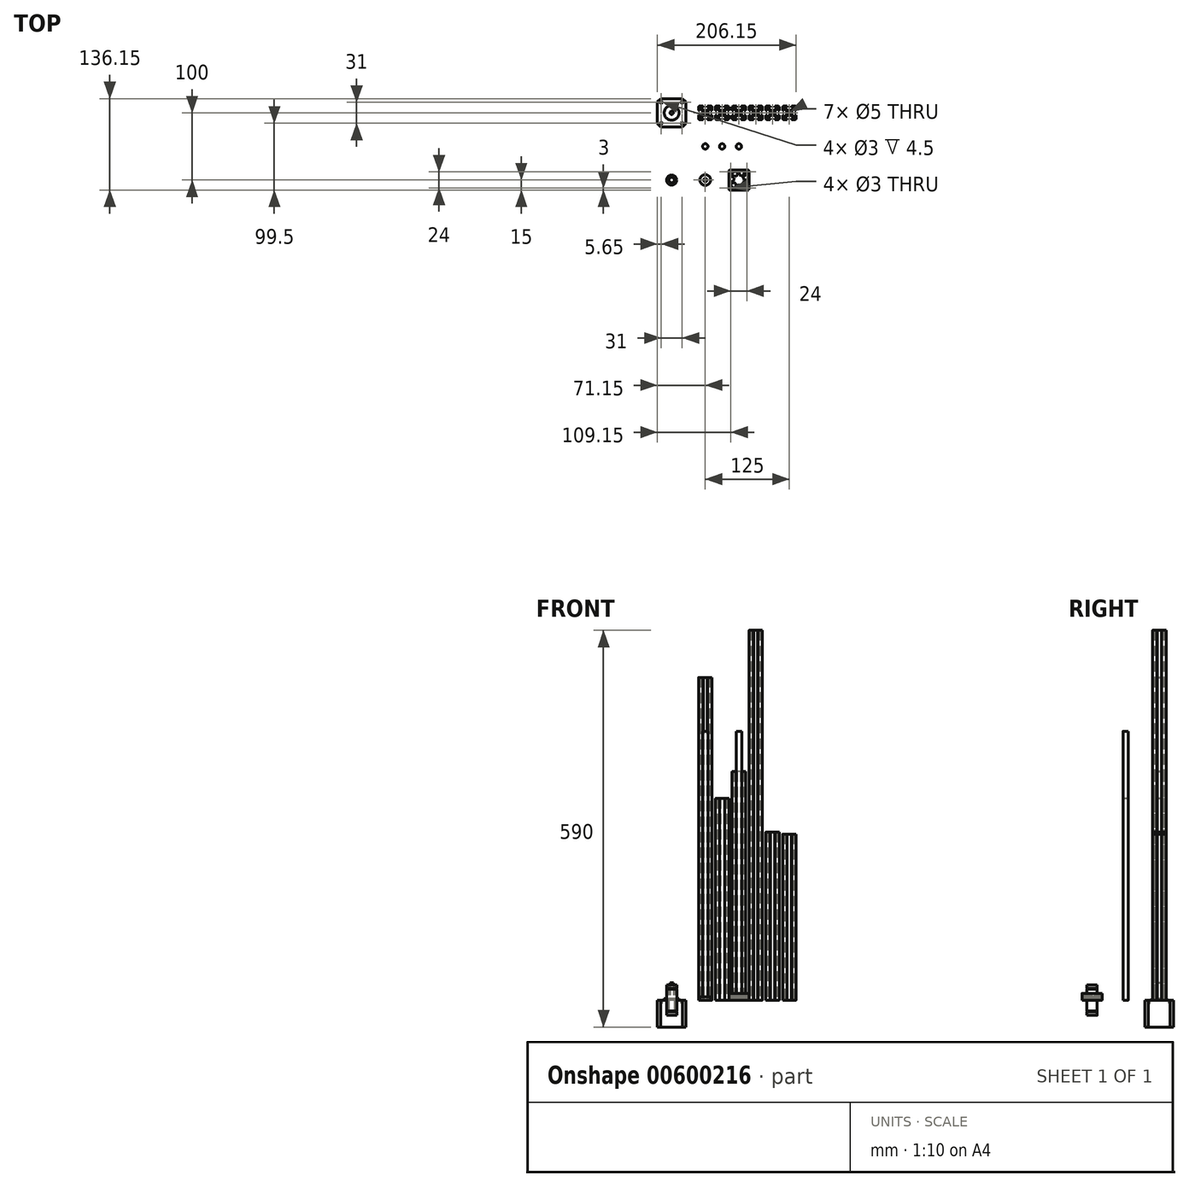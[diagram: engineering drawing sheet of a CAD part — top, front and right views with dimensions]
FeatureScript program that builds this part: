
annotation { "Feature Type Name" : "Feature", "Feature Type Description" : "" }
export const myFeature = defineFeature(function(context is Context, id is Id, definition is map)
    precondition{}
    {
        {
            assignVariable(context, id + "F0", {"name" : "X", "anyValue" : 480});
        }
        {
            assignVariable(context, id + "F1", {"name" : "Y", "anyValue" : 300});
        }
        {
            assignVariable(context, id + "F2", {"name" : "Z", "anyValue" : 550});
        }
        {
            var Q0;
            Q0=qCreatedBy(makeId("Top.planeOp"),FACE);
            var sketch = newSketch(context, id + "F3", { "sketchPlane" : qUnion([Q0])});
            skLineSegment(sketch, "E0.bottom", {"start": v(8.5, -10) * mm, "end": v(-8.5, -10) * mm});
            skLineSegment(sketch, "E0.top", {"start": v(8.5, 10) * mm, "end": v(-8.5, 10) * mm});
            skLineSegment(sketch, "E0.left", {"start": v(10, -8.5) * mm, "end": v(10, 8.5) * mm});
            skLineSegment(sketch, "E0.right", {"start": v(-10, -8.5) * mm, "end": v(-10, 8.5) * mm});
            skPoint(sketch, "E0.middle", {"position": v(0, 0) * mm});
            skPoint(sketch, "E1.visualSharp", {"position": v(-10, 10) * mm});
            skArc(sketch, "E1.filletArc", {"start": v(-8.5, 10) * mm, "mid": v(-9.56, 9.56) * mm, "end": v(-10, 8.5) * mm});
            skPoint(sketch, "E2.visualSharp", {"position": v(10, 10) * mm});
            skArc(sketch, "E2.filletArc", {"start": v(10, 8.5) * mm, "mid": v(9.56, 9.56) * mm, "end": v(8.5, 10) * mm});
            skPoint(sketch, "E3.visualSharp", {"position": v(10, -10) * mm});
            skArc(sketch, "E3.filletArc", {"start": v(8.5, -10) * mm, "mid": v(9.56, -9.56) * mm, "end": v(10, -8.5) * mm});
            skPoint(sketch, "E4.visualSharp", {"position": v(-10, -10) * mm});
            skArc(sketch, "E4.filletArc", {"start": v(-10, -8.5) * mm, "mid": v(-9.56, -9.56) * mm, "end": v(-8.5, -10) * mm});
            skCircle(sketch, "E5", {"center": v(0, 0) * mm, "radius": 2.5 * mm});
            skLineSegment(sketch, "E6", {"start": v(-3.6, -10) * mm, "end": v(-3.6, -9.7) * mm});
            skLineSegment(sketch, "E7", {"start": v(-3.4, -9.5) * mm, "end": v(-3.1, -9.5) * mm});
            skLineSegment(sketch, "E8", {"start": v(-3.1, -9.5) * mm, "end": v(-3.1, -8.2) * mm});
            skLineSegment(sketch, "E9", {"start": v(-3.1, -8.2) * mm, "end": v(-5.5, -8.2) * mm});
            skLineSegment(sketch, "E10", {"start": v(-3.43, -4.49) * mm, "end": v(-5.5, -6.56) * mm});
            skLineSegment(sketch, "E11", {"start": v(-2.01, -3.9) * mm, "end": v(2.01, -3.9) * mm});
            skLineSegment(sketch, "E12", {"start": v(5.5, -6.56) * mm, "end": v(3.43, -4.49) * mm});
            skLineSegment(sketch, "E13", {"start": v(5.5, -8.2) * mm, "end": v(3.1, -8.2) * mm});
            skLineSegment(sketch, "E14", {"start": v(3.1, -8.2) * mm, "end": v(3.1, -9.5) * mm});
            skLineSegment(sketch, "E15", {"start": v(3.1, -9.5) * mm, "end": v(3.4, -9.5) * mm});
            skLineSegment(sketch, "E16", {"start": v(3.6, -9.7) * mm, "end": v(3.6, -10) * mm});
            skLineSegment(sketch, "E17", {"start": v(0, 0) * mm, "end": v(0, -10) * mm, "construction": true});
            skLineSegment(sketch, "E18", {"start": v(5.5, -6.56) * mm, "end": v(5.5, -8.2) * mm});
            skLineSegment(sketch, "E19", {"start": v(-5.5, -6.56) * mm, "end": v(-5.5, -8.2) * mm});
            skPoint(sketch, "E20.visualSharp", {"position": v(-2.84, -3.9) * mm});
            skArc(sketch, "E20.filletArc", {"start": v(-2.01, -3.9) * mm, "mid": v(-2.78, -4.05) * mm, "end": v(-3.43, -4.49) * mm});
            skPoint(sketch, "E21.visualSharp", {"position": v(2.84, -3.9) * mm});
            skArc(sketch, "E21.filletArc", {"start": v(3.43, -4.49) * mm, "mid": v(2.78, -4.05) * mm, "end": v(2.01, -3.9) * mm});
            skPoint(sketch, "E22.visualSharp", {"position": v(-3.6, -9.5) * mm});
            skArc(sketch, "E22.filletArc", {"start": v(-3.4, -9.5) * mm, "mid": v(-3.54, -9.56) * mm, "end": v(-3.6, -9.7) * mm});
            skPoint(sketch, "E23.visualSharp", {"position": v(3.6, -9.5) * mm});
            skArc(sketch, "E23.filletArc", {"start": v(3.6, -9.7) * mm, "mid": v(3.54, -9.56) * mm, "end": v(3.4, -9.5) * mm});
            skLineSegment(sketch, "E24.1.0", {"start": v(6.56, 5.5) * mm, "end": v(4.49, 3.43) * mm});
            skLineSegment(sketch, "E24.1.1", {"start": v(3.9, -2.01) * mm, "end": v(3.9, 2.01) * mm});
            skLineSegment(sketch, "E24.1.2", {"start": v(6.56, 5.5) * mm, "end": v(8.2, 5.5) * mm});
            skArc(sketch, "E24.1.3", {"start": v(4.49, 3.43) * mm, "mid": v(4.05, 2.78) * mm, "end": v(3.9, 2.01) * mm});
            skLineSegment(sketch, "E24.1.4", {"start": v(8.2, 3.1) * mm, "end": v(9.5, 3.1) * mm});
            skPoint(sketch, "E24.1.5", {"position": v(3.9, -2.84) * mm});
            skPoint(sketch, "E24.1.6", {"position": v(9.5, -3.6) * mm});
            skPoint(sketch, "E24.1.7", {"position": v(9.5, 3.6) * mm});
            skLineSegment(sketch, "E24.1.8", {"start": v(8.2, -3.1) * mm, "end": v(8.2, -5.5) * mm});
            skLineSegment(sketch, "E24.1.9", {"start": v(9.7, 3.6) * mm, "end": v(10, 3.6) * mm});
            skLineSegment(sketch, "E24.1.10", {"start": v(9.5, -3.1) * mm, "end": v(8.2, -3.1) * mm});
            skLineSegment(sketch, "E24.1.11", {"start": v(8.2, 5.5) * mm, "end": v(8.2, 3.1) * mm});
            skLineSegment(sketch, "E24.1.12", {"start": v(4.49, -3.43) * mm, "end": v(6.56, -5.5) * mm});
            skPoint(sketch, "E24.1.13", {"position": v(3.9, 2.84) * mm});
            skLineSegment(sketch, "E24.1.14", {"start": v(6.56, -5.5) * mm, "end": v(8.2, -5.5) * mm});
            skLineSegment(sketch, "E24.1.15", {"start": v(9.5, 3.1) * mm, "end": v(9.5, 3.4) * mm});
            skLineSegment(sketch, "E24.1.16", {"start": v(9.5, -3.4) * mm, "end": v(9.5, -3.1) * mm});
            skArc(sketch, "E24.1.17", {"start": v(3.9, -2.01) * mm, "mid": v(4.05, -2.78) * mm, "end": v(4.49, -3.43) * mm});
            skLineSegment(sketch, "E24.1.18", {"start": v(10, -3.6) * mm, "end": v(9.7, -3.6) * mm});
            skArc(sketch, "E24.1.19", {"start": v(9.5, -3.4) * mm, "mid": v(9.56, -3.54) * mm, "end": v(9.7, -3.6) * mm});
            skArc(sketch, "E24.1.20", {"start": v(9.7, 3.6) * mm, "mid": v(9.56, 3.54) * mm, "end": v(9.5, 3.4) * mm});
            skLineSegment(sketch, "E24.2.0", {"start": v(-5.5, 6.56) * mm, "end": v(-3.43, 4.49) * mm});
            skLineSegment(sketch, "E24.2.1", {"start": v(2.01, 3.9) * mm, "end": v(-2.01, 3.9) * mm});
            skLineSegment(sketch, "E24.2.2", {"start": v(-5.5, 6.56) * mm, "end": v(-5.5, 8.2) * mm});
            skArc(sketch, "E24.2.3", {"start": v(-3.43, 4.49) * mm, "mid": v(-2.78, 4.05) * mm, "end": v(-2.01, 3.9) * mm});
            skLineSegment(sketch, "E24.2.4", {"start": v(-3.1, 8.2) * mm, "end": v(-3.1, 9.5) * mm});
            skPoint(sketch, "E24.2.5", {"position": v(2.84, 3.9) * mm});
            skPoint(sketch, "E24.2.6", {"position": v(3.6, 9.5) * mm});
            skPoint(sketch, "E24.2.7", {"position": v(-3.6, 9.5) * mm});
            skLineSegment(sketch, "E24.2.8", {"start": v(3.1, 8.2) * mm, "end": v(5.5, 8.2) * mm});
            skLineSegment(sketch, "E24.2.9", {"start": v(-3.6, 9.7) * mm, "end": v(-3.6, 10) * mm});
            skLineSegment(sketch, "E24.2.10", {"start": v(3.1, 9.5) * mm, "end": v(3.1, 8.2) * mm});
            skLineSegment(sketch, "E24.2.11", {"start": v(-5.5, 8.2) * mm, "end": v(-3.1, 8.2) * mm});
            skLineSegment(sketch, "E24.2.12", {"start": v(3.43, 4.49) * mm, "end": v(5.5, 6.56) * mm});
            skPoint(sketch, "E24.2.13", {"position": v(-2.84, 3.9) * mm});
            skLineSegment(sketch, "E24.2.14", {"start": v(5.5, 6.56) * mm, "end": v(5.5, 8.2) * mm});
            skLineSegment(sketch, "E24.2.15", {"start": v(-3.1, 9.5) * mm, "end": v(-3.4, 9.5) * mm});
            skLineSegment(sketch, "E24.2.16", {"start": v(3.4, 9.5) * mm, "end": v(3.1, 9.5) * mm});
            skArc(sketch, "E24.2.17", {"start": v(2.01, 3.9) * mm, "mid": v(2.78, 4.05) * mm, "end": v(3.43, 4.49) * mm});
            skLineSegment(sketch, "E24.2.18", {"start": v(3.6, 10) * mm, "end": v(3.6, 9.7) * mm});
            skArc(sketch, "E24.2.19", {"start": v(3.4, 9.5) * mm, "mid": v(3.54, 9.56) * mm, "end": v(3.6, 9.7) * mm});
            skArc(sketch, "E24.2.20", {"start": v(-3.6, 9.7) * mm, "mid": v(-3.54, 9.56) * mm, "end": v(-3.4, 9.5) * mm});
            skLineSegment(sketch, "E24.3.0", {"start": v(-6.56, -5.5) * mm, "end": v(-4.49, -3.43) * mm});
            skLineSegment(sketch, "E24.3.1", {"start": v(-3.9, 2.01) * mm, "end": v(-3.9, -2.01) * mm});
            skLineSegment(sketch, "E24.3.2", {"start": v(-6.56, -5.5) * mm, "end": v(-8.2, -5.5) * mm});
            skArc(sketch, "E24.3.3", {"start": v(-4.49, -3.43) * mm, "mid": v(-4.05, -2.78) * mm, "end": v(-3.9, -2.01) * mm});
            skLineSegment(sketch, "E24.3.4", {"start": v(-8.2, -3.1) * mm, "end": v(-9.5, -3.1) * mm});
            skPoint(sketch, "E24.3.5", {"position": v(-3.9, 2.84) * mm});
            skPoint(sketch, "E24.3.6", {"position": v(-9.5, 3.6) * mm});
            skPoint(sketch, "E24.3.7", {"position": v(-9.5, -3.6) * mm});
            skLineSegment(sketch, "E24.3.8", {"start": v(-8.2, 3.1) * mm, "end": v(-8.2, 5.5) * mm});
            skLineSegment(sketch, "E24.3.9", {"start": v(-9.7, -3.6) * mm, "end": v(-10, -3.6) * mm});
            skLineSegment(sketch, "E24.3.10", {"start": v(-9.5, 3.1) * mm, "end": v(-8.2, 3.1) * mm});
            skLineSegment(sketch, "E24.3.11", {"start": v(-8.2, -5.5) * mm, "end": v(-8.2, -3.1) * mm});
            skLineSegment(sketch, "E24.3.12", {"start": v(-4.49, 3.43) * mm, "end": v(-6.56, 5.5) * mm});
            skPoint(sketch, "E24.3.13", {"position": v(-3.9, -2.84) * mm});
            skLineSegment(sketch, "E24.3.14", {"start": v(-6.56, 5.5) * mm, "end": v(-8.2, 5.5) * mm});
            skLineSegment(sketch, "E24.3.15", {"start": v(-9.5, -3.1) * mm, "end": v(-9.5, -3.4) * mm});
            skLineSegment(sketch, "E24.3.16", {"start": v(-9.5, 3.4) * mm, "end": v(-9.5, 3.1) * mm});
            skArc(sketch, "E24.3.17", {"start": v(-3.9, 2.01) * mm, "mid": v(-4.05, 2.78) * mm, "end": v(-4.49, 3.43) * mm});
            skLineSegment(sketch, "E24.3.18", {"start": v(-10, 3.6) * mm, "end": v(-9.7, 3.6) * mm});
            skArc(sketch, "E24.3.19", {"start": v(-9.5, 3.4) * mm, "mid": v(-9.56, 3.54) * mm, "end": v(-9.7, 3.6) * mm});
            skArc(sketch, "E24.3.20", {"start": v(-9.7, -3.6) * mm, "mid": v(-9.56, -3.54) * mm, "end": v(-9.5, -3.4) * mm});
            skLineSegment(sketch, "E25.1.0.0", {"start": v(33.5, 10) * mm, "end": v(16.5, 10) * mm});
            skLineSegment(sketch, "E25.1.0.1", {"start": v(35, -8.5) * mm, "end": v(35, 8.5) * mm});
            skLineSegment(sketch, "E25.1.0.2", {"start": v(33.5, -10) * mm, "end": v(16.5, -10) * mm});
            skLineSegment(sketch, "E25.1.0.3", {"start": v(30.5, -6.56) * mm, "end": v(28.43, -4.49) * mm});
            skLineSegment(sketch, "E25.1.0.4", {"start": v(15, -8.5) * mm, "end": v(15, 8.5) * mm});
            skPoint(sketch, "E25.1.0.5", {"position": v(15, 10) * mm});
            skPoint(sketch, "E25.1.0.6", {"position": v(35, -10) * mm});
            skCircle(sketch, "E25.1.0.7", {"center": v(25, 0) * mm, "radius": 2.5 * mm});
            skLineSegment(sketch, "E25.1.0.8", {"start": v(28.1, 8.2) * mm, "end": v(30.5, 8.2) * mm});
            skPoint(sketch, "E25.1.0.9", {"position": v(21.1, -2.84) * mm});
            skPoint(sketch, "E25.1.0.10", {"position": v(28.9, 2.84) * mm});
            skLineSegment(sketch, "E25.1.0.11", {"start": v(18.44, -5.5) * mm, "end": v(20.51, -3.43) * mm});
            skLineSegment(sketch, "E25.1.0.12", {"start": v(30.5, -8.2) * mm, "end": v(28.1, -8.2) * mm});
            skPoint(sketch, "E25.1.0.13", {"position": v(15, -10) * mm});
            skLineSegment(sketch, "E25.1.0.14", {"start": v(22.99, -3.9) * mm, "end": v(27.01, -3.9) * mm});
            skLineSegment(sketch, "E25.1.0.15", {"start": v(27.01, 3.9) * mm, "end": v(22.99, 3.9) * mm});
            skLineSegment(sketch, "E25.1.0.16", {"start": v(31.56, 5.5) * mm, "end": v(29.49, 3.43) * mm});
            skPoint(sketch, "E25.1.0.17", {"position": v(15.5, 3.6) * mm});
            skPoint(sketch, "E25.1.0.18", {"position": v(34.5, -3.6) * mm});
            skLineSegment(sketch, "E25.1.0.19", {"start": v(33.2, -3.1) * mm, "end": v(33.2, -5.5) * mm});
            skLineSegment(sketch, "E25.1.0.20", {"start": v(21.57, -4.49) * mm, "end": v(19.5, -6.56) * mm});
            skPoint(sketch, "E25.1.0.21", {"position": v(15.5, -3.6) * mm});
            skPoint(sketch, "E25.1.0.22", {"position": v(34.5, 3.6) * mm});
            skLineSegment(sketch, "E25.1.0.23", {"start": v(19.5, 6.56) * mm, "end": v(21.57, 4.49) * mm});
            skLineSegment(sketch, "E25.1.0.24", {"start": v(28.9, -2.01) * mm, "end": v(28.9, 2.01) * mm});
            skLineSegment(sketch, "E25.1.0.25", {"start": v(21.1, 2.01) * mm, "end": v(21.1, -2.01) * mm});
            skLineSegment(sketch, "E25.1.0.26", {"start": v(16.8, 3.1) * mm, "end": v(16.8, 5.5) * mm});
            skPoint(sketch, "E25.1.0.27", {"position": v(35, 10) * mm});
            skPoint(sketch, "E25.1.0.28", {"position": v(28.9, -2.84) * mm});
            skPoint(sketch, "E25.1.0.29", {"position": v(21.1, 2.84) * mm});
            skPoint(sketch, "E25.1.0.30", {"position": v(25, 0) * mm});
            skPoint(sketch, "E25.1.0.31", {"position": v(28.6, -9.5) * mm});
            skPoint(sketch, "E25.1.0.32", {"position": v(22.16, 3.9) * mm});
            skPoint(sketch, "E25.1.0.33", {"position": v(21.4, 9.5) * mm});
            skLineSegment(sketch, "E25.1.0.34", {"start": v(20.51, 3.43) * mm, "end": v(18.44, 5.5) * mm});
            skPoint(sketch, "E25.1.0.35", {"position": v(27.84, -3.9) * mm});
            skPoint(sketch, "E25.1.0.36", {"position": v(28.6, 9.5) * mm});
            skLineSegment(sketch, "E25.1.0.37", {"start": v(28.43, 4.49) * mm, "end": v(30.5, 6.56) * mm});
            skLineSegment(sketch, "E25.1.0.38", {"start": v(16.8, -5.5) * mm, "end": v(16.8, -3.1) * mm});
            skPoint(sketch, "E25.1.0.39", {"position": v(27.84, 3.9) * mm});
            skLineSegment(sketch, "E25.1.0.40", {"start": v(29.49, -3.43) * mm, "end": v(31.56, -5.5) * mm});
            skLineSegment(sketch, "E25.1.0.41", {"start": v(19.5, 8.2) * mm, "end": v(21.9, 8.2) * mm});
            skLineSegment(sketch, "E25.1.0.42", {"start": v(25, 0) * mm, "end": v(25, -10) * mm, "construction": true});
            skPoint(sketch, "E25.1.0.43", {"position": v(22.16, -3.9) * mm});
            skLineSegment(sketch, "E25.1.0.44", {"start": v(33.2, 5.5) * mm, "end": v(33.2, 3.1) * mm});
            skArc(sketch, "E25.1.0.45", {"start": v(35, 8.5) * mm, "mid": v(34.56, 9.56) * mm, "end": v(33.5, 10) * mm});
            skArc(sketch, "E25.1.0.46", {"start": v(16.5, 10) * mm, "mid": v(15.44, 9.56) * mm, "end": v(15, 8.5) * mm});
            skLineSegment(sketch, "E25.1.0.47", {"start": v(21.9, -8.2) * mm, "end": v(19.5, -8.2) * mm});
            skArc(sketch, "E25.1.0.48", {"start": v(33.5, -10) * mm, "mid": v(34.56, -9.56) * mm, "end": v(35, -8.5) * mm});
            skArc(sketch, "E25.1.0.49", {"start": v(15, -8.5) * mm, "mid": v(15.44, -9.56) * mm, "end": v(16.5, -10) * mm});
            skPoint(sketch, "E25.1.0.50", {"position": v(21.4, -9.5) * mm});
            skPoint(sketch, "E25.1.0.51", {"position": v(25, 0) * mm});
            skLineSegment(sketch, "E25.1.0.52", {"start": v(28.1, -8.2) * mm, "end": v(28.1, -9.5) * mm});
            skLineSegment(sketch, "E25.1.0.53", {"start": v(16.8, -3.1) * mm, "end": v(15.5, -3.1) * mm});
            skLineSegment(sketch, "E25.1.0.54", {"start": v(18.44, -5.5) * mm, "end": v(16.8, -5.5) * mm});
            skArc(sketch, "E25.1.0.55", {"start": v(20.51, -3.43) * mm, "mid": v(20.95, -2.78) * mm, "end": v(21.1, -2.01) * mm});
            skLineSegment(sketch, "E25.1.0.56", {"start": v(21.9, 8.2) * mm, "end": v(21.9, 9.5) * mm});
            skLineSegment(sketch, "E25.1.0.57", {"start": v(33.2, 3.1) * mm, "end": v(34.5, 3.1) * mm});
            skLineSegment(sketch, "E25.1.0.58", {"start": v(31.56, 5.5) * mm, "end": v(33.2, 5.5) * mm});
            skArc(sketch, "E25.1.0.59", {"start": v(21.57, 4.49) * mm, "mid": v(22.22, 4.05) * mm, "end": v(22.99, 3.9) * mm});
            skLineSegment(sketch, "E25.1.0.60", {"start": v(19.5, 6.56) * mm, "end": v(19.5, 8.2) * mm});
            skLineSegment(sketch, "E25.1.0.61", {"start": v(34.5, -3.1) * mm, "end": v(33.2, -3.1) * mm});
            skArc(sketch, "E25.1.0.62", {"start": v(29.49, 3.43) * mm, "mid": v(29.05, 2.78) * mm, "end": v(28.9, 2.01) * mm});
            skArc(sketch, "E25.1.0.63", {"start": v(21.1, 2.01) * mm, "mid": v(20.95, 2.78) * mm, "end": v(20.51, 3.43) * mm});
            skArc(sketch, "E25.1.0.64", {"start": v(27.01, 3.9) * mm, "mid": v(27.78, 4.05) * mm, "end": v(28.43, 4.49) * mm});
            skArc(sketch, "E25.1.0.65", {"start": v(28.43, -4.49) * mm, "mid": v(27.78, -4.05) * mm, "end": v(27.01, -3.9) * mm});
            skArc(sketch, "E25.1.0.66", {"start": v(28.9, -2.01) * mm, "mid": v(29.05, -2.78) * mm, "end": v(29.49, -3.43) * mm});
            skLineSegment(sketch, "E25.1.0.67", {"start": v(18.44, 5.5) * mm, "end": v(16.8, 5.5) * mm});
            skArc(sketch, "E25.1.0.68", {"start": v(22.99, -3.9) * mm, "mid": v(22.22, -4.05) * mm, "end": v(21.57, -4.49) * mm});
            skLineSegment(sketch, "E25.1.0.69", {"start": v(30.5, 6.56) * mm, "end": v(30.5, 8.2) * mm});
            skLineSegment(sketch, "E25.1.0.70", {"start": v(19.5, -6.56) * mm, "end": v(19.5, -8.2) * mm});
            skLineSegment(sketch, "E25.1.0.71", {"start": v(31.56, -5.5) * mm, "end": v(33.2, -5.5) * mm});
            skLineSegment(sketch, "E25.1.0.72", {"start": v(30.5, -6.56) * mm, "end": v(30.5, -8.2) * mm});
            skLineSegment(sketch, "E25.1.0.73", {"start": v(15.5, 3.1) * mm, "end": v(16.8, 3.1) * mm});
            skLineSegment(sketch, "E25.1.0.74", {"start": v(28.1, 9.5) * mm, "end": v(28.1, 8.2) * mm});
            skLineSegment(sketch, "E25.1.0.75", {"start": v(21.9, -9.5) * mm, "end": v(21.9, -8.2) * mm});
            skArc(sketch, "E25.1.0.76", {"start": v(34.5, -3.4) * mm, "mid": v(34.56, -3.54) * mm, "end": v(34.7, -3.6) * mm});
            skLineSegment(sketch, "E25.1.0.77", {"start": v(35, -3.6) * mm, "end": v(34.7, -3.6) * mm});
            skLineSegment(sketch, "E25.1.0.78", {"start": v(34.5, -3.4) * mm, "end": v(34.5, -3.1) * mm});
            skArc(sketch, "E25.1.0.79", {"start": v(15.3, -3.6) * mm, "mid": v(15.44, -3.54) * mm, "end": v(15.5, -3.4) * mm});
            skArc(sketch, "E25.1.0.80", {"start": v(28.4, 9.5) * mm, "mid": v(28.54, 9.56) * mm, "end": v(28.6, 9.7) * mm});
            skLineSegment(sketch, "E25.1.0.81", {"start": v(28.1, -9.5) * mm, "end": v(28.4, -9.5) * mm});
            skArc(sketch, "E25.1.0.82", {"start": v(28.6, -9.7) * mm, "mid": v(28.54, -9.56) * mm, "end": v(28.4, -9.5) * mm});
            skLineSegment(sketch, "E25.1.0.83", {"start": v(28.6, 10) * mm, "end": v(28.6, 9.7) * mm});
            skLineSegment(sketch, "E25.1.0.84", {"start": v(15.5, -3.1) * mm, "end": v(15.5, -3.4) * mm});
            skLineSegment(sketch, "E25.1.0.85", {"start": v(28.4, 9.5) * mm, "end": v(28.1, 9.5) * mm});
            skLineSegment(sketch, "E25.1.0.86", {"start": v(15.3, -3.6) * mm, "end": v(15, -3.6) * mm});
            skLineSegment(sketch, "E25.1.0.87", {"start": v(28.6, -9.7) * mm, "end": v(28.6, -10) * mm});
            skArc(sketch, "E25.1.0.88", {"start": v(21.4, 9.7) * mm, "mid": v(21.46, 9.56) * mm, "end": v(21.6, 9.5) * mm});
            skLineSegment(sketch, "E25.1.0.89", {"start": v(21.4, -10) * mm, "end": v(21.4, -9.7) * mm});
            skLineSegment(sketch, "E25.1.0.90", {"start": v(21.6, -9.5) * mm, "end": v(21.9, -9.5) * mm});
            skLineSegment(sketch, "E25.1.0.91", {"start": v(21.4, 9.7) * mm, "end": v(21.4, 10) * mm});
            skLineSegment(sketch, "E25.1.0.92", {"start": v(21.9, 9.5) * mm, "end": v(21.6, 9.5) * mm});
            skLineSegment(sketch, "E25.1.0.93", {"start": v(15, 3.6) * mm, "end": v(15.3, 3.6) * mm});
            skArc(sketch, "E25.1.0.94", {"start": v(34.7, 3.6) * mm, "mid": v(34.56, 3.54) * mm, "end": v(34.5, 3.4) * mm});
            skArc(sketch, "E25.1.0.95", {"start": v(15.5, 3.4) * mm, "mid": v(15.44, 3.54) * mm, "end": v(15.3, 3.6) * mm});
            skLineSegment(sketch, "E25.1.0.96", {"start": v(34.7, 3.6) * mm, "end": v(35, 3.6) * mm});
            skLineSegment(sketch, "E25.1.0.97", {"start": v(15.5, 3.4) * mm, "end": v(15.5, 3.1) * mm});
            skArc(sketch, "E25.1.0.98", {"start": v(21.6, -9.5) * mm, "mid": v(21.46, -9.56) * mm, "end": v(21.4, -9.7) * mm});
            skLineSegment(sketch, "E25.1.0.99", {"start": v(34.5, 3.1) * mm, "end": v(34.5, 3.4) * mm});
            skLineSegment(sketch, "E25.2.0.0", {"start": v(58.5, 10) * mm, "end": v(41.5, 10) * mm});
            skLineSegment(sketch, "E25.2.0.1", {"start": v(60, -8.5) * mm, "end": v(60, 8.5) * mm});
            skLineSegment(sketch, "E25.2.0.2", {"start": v(58.5, -10) * mm, "end": v(41.5, -10) * mm});
            skLineSegment(sketch, "E25.2.0.3", {"start": v(55.5, -6.56) * mm, "end": v(53.43, -4.49) * mm});
            skLineSegment(sketch, "E25.2.0.4", {"start": v(40, -8.5) * mm, "end": v(40, 8.5) * mm});
            skPoint(sketch, "E25.2.0.5", {"position": v(40, 10) * mm});
            skPoint(sketch, "E25.2.0.6", {"position": v(60, -10) * mm});
            skCircle(sketch, "E25.2.0.7", {"center": v(50, 0) * mm, "radius": 2.5 * mm});
            skLineSegment(sketch, "E25.2.0.8", {"start": v(53.1, 8.2) * mm, "end": v(55.5, 8.2) * mm});
            skPoint(sketch, "E25.2.0.9", {"position": v(46.1, -2.84) * mm});
            skPoint(sketch, "E25.2.0.10", {"position": v(53.9, 2.84) * mm});
            skLineSegment(sketch, "E25.2.0.11", {"start": v(43.44, -5.5) * mm, "end": v(45.51, -3.43) * mm});
            skLineSegment(sketch, "E25.2.0.12", {"start": v(55.5, -8.2) * mm, "end": v(53.1, -8.2) * mm});
            skPoint(sketch, "E25.2.0.13", {"position": v(40, -10) * mm});
            skLineSegment(sketch, "E25.2.0.14", {"start": v(47.99, -3.9) * mm, "end": v(52.01, -3.9) * mm});
            skLineSegment(sketch, "E25.2.0.15", {"start": v(52.01, 3.9) * mm, "end": v(47.99, 3.9) * mm});
            skLineSegment(sketch, "E25.2.0.16", {"start": v(56.56, 5.5) * mm, "end": v(54.49, 3.43) * mm});
            skPoint(sketch, "E25.2.0.17", {"position": v(40.5, 3.6) * mm});
            skPoint(sketch, "E25.2.0.18", {"position": v(59.5, -3.6) * mm});
            skLineSegment(sketch, "E25.2.0.19", {"start": v(58.2, -3.1) * mm, "end": v(58.2, -5.5) * mm});
            skLineSegment(sketch, "E25.2.0.20", {"start": v(46.57, -4.49) * mm, "end": v(44.5, -6.56) * mm});
            skPoint(sketch, "E25.2.0.21", {"position": v(40.5, -3.6) * mm});
            skPoint(sketch, "E25.2.0.22", {"position": v(59.5, 3.6) * mm});
            skLineSegment(sketch, "E25.2.0.23", {"start": v(44.5, 6.56) * mm, "end": v(46.57, 4.49) * mm});
            skLineSegment(sketch, "E25.2.0.24", {"start": v(53.9, -2.01) * mm, "end": v(53.9, 2.01) * mm});
            skLineSegment(sketch, "E25.2.0.25", {"start": v(46.1, 2.01) * mm, "end": v(46.1, -2.01) * mm});
            skLineSegment(sketch, "E25.2.0.26", {"start": v(41.8, 3.1) * mm, "end": v(41.8, 5.5) * mm});
            skPoint(sketch, "E25.2.0.27", {"position": v(60, 10) * mm});
            skPoint(sketch, "E25.2.0.28", {"position": v(53.9, -2.84) * mm});
            skPoint(sketch, "E25.2.0.29", {"position": v(46.1, 2.84) * mm});
            skPoint(sketch, "E25.2.0.30", {"position": v(50, 0) * mm});
            skPoint(sketch, "E25.2.0.31", {"position": v(53.6, -9.5) * mm});
            skPoint(sketch, "E25.2.0.32", {"position": v(47.16, 3.9) * mm});
            skPoint(sketch, "E25.2.0.33", {"position": v(46.4, 9.5) * mm});
            skLineSegment(sketch, "E25.2.0.34", {"start": v(45.51, 3.43) * mm, "end": v(43.44, 5.5) * mm});
            skPoint(sketch, "E25.2.0.35", {"position": v(52.84, -3.9) * mm});
            skPoint(sketch, "E25.2.0.36", {"position": v(53.6, 9.5) * mm});
            skLineSegment(sketch, "E25.2.0.37", {"start": v(53.43, 4.49) * mm, "end": v(55.5, 6.56) * mm});
            skLineSegment(sketch, "E25.2.0.38", {"start": v(41.8, -5.5) * mm, "end": v(41.8, -3.1) * mm});
            skPoint(sketch, "E25.2.0.39", {"position": v(52.84, 3.9) * mm});
            skLineSegment(sketch, "E25.2.0.40", {"start": v(54.49, -3.43) * mm, "end": v(56.56, -5.5) * mm});
            skLineSegment(sketch, "E25.2.0.41", {"start": v(44.5, 8.2) * mm, "end": v(46.9, 8.2) * mm});
            skLineSegment(sketch, "E25.2.0.42", {"start": v(50, 0) * mm, "end": v(50, -10) * mm, "construction": true});
            skPoint(sketch, "E25.2.0.43", {"position": v(47.16, -3.9) * mm});
            skLineSegment(sketch, "E25.2.0.44", {"start": v(58.2, 5.5) * mm, "end": v(58.2, 3.1) * mm});
            skArc(sketch, "E25.2.0.45", {"start": v(60, 8.5) * mm, "mid": v(59.56, 9.56) * mm, "end": v(58.5, 10) * mm});
            skArc(sketch, "E25.2.0.46", {"start": v(41.5, 10) * mm, "mid": v(40.44, 9.56) * mm, "end": v(40, 8.5) * mm});
            skLineSegment(sketch, "E25.2.0.47", {"start": v(46.9, -8.2) * mm, "end": v(44.5, -8.2) * mm});
            skArc(sketch, "E25.2.0.48", {"start": v(58.5, -10) * mm, "mid": v(59.56, -9.56) * mm, "end": v(60, -8.5) * mm});
            skArc(sketch, "E25.2.0.49", {"start": v(40, -8.5) * mm, "mid": v(40.44, -9.56) * mm, "end": v(41.5, -10) * mm});
            skPoint(sketch, "E25.2.0.50", {"position": v(46.4, -9.5) * mm});
            skPoint(sketch, "E25.2.0.51", {"position": v(50, 0) * mm});
            skLineSegment(sketch, "E25.2.0.52", {"start": v(53.1, -8.2) * mm, "end": v(53.1, -9.5) * mm});
            skLineSegment(sketch, "E25.2.0.53", {"start": v(41.8, -3.1) * mm, "end": v(40.5, -3.1) * mm});
            skLineSegment(sketch, "E25.2.0.54", {"start": v(43.44, -5.5) * mm, "end": v(41.8, -5.5) * mm});
            skArc(sketch, "E25.2.0.55", {"start": v(45.51, -3.43) * mm, "mid": v(45.95, -2.78) * mm, "end": v(46.1, -2.01) * mm});
            skLineSegment(sketch, "E25.2.0.56", {"start": v(46.9, 8.2) * mm, "end": v(46.9, 9.5) * mm});
            skLineSegment(sketch, "E25.2.0.57", {"start": v(58.2, 3.1) * mm, "end": v(59.5, 3.1) * mm});
            skLineSegment(sketch, "E25.2.0.58", {"start": v(56.56, 5.5) * mm, "end": v(58.2, 5.5) * mm});
            skArc(sketch, "E25.2.0.59", {"start": v(46.57, 4.49) * mm, "mid": v(47.22, 4.05) * mm, "end": v(47.99, 3.9) * mm});
            skLineSegment(sketch, "E25.2.0.60", {"start": v(44.5, 6.56) * mm, "end": v(44.5, 8.2) * mm});
            skLineSegment(sketch, "E25.2.0.61", {"start": v(59.5, -3.1) * mm, "end": v(58.2, -3.1) * mm});
            skArc(sketch, "E25.2.0.62", {"start": v(54.49, 3.43) * mm, "mid": v(54.05, 2.78) * mm, "end": v(53.9, 2.01) * mm});
            skArc(sketch, "E25.2.0.63", {"start": v(46.1, 2.01) * mm, "mid": v(45.95, 2.78) * mm, "end": v(45.51, 3.43) * mm});
            skArc(sketch, "E25.2.0.64", {"start": v(52.01, 3.9) * mm, "mid": v(52.78, 4.05) * mm, "end": v(53.43, 4.49) * mm});
            skArc(sketch, "E25.2.0.65", {"start": v(53.43, -4.49) * mm, "mid": v(52.78, -4.05) * mm, "end": v(52.01, -3.9) * mm});
            skArc(sketch, "E25.2.0.66", {"start": v(53.9, -2.01) * mm, "mid": v(54.05, -2.78) * mm, "end": v(54.49, -3.43) * mm});
            skLineSegment(sketch, "E25.2.0.67", {"start": v(43.44, 5.5) * mm, "end": v(41.8, 5.5) * mm});
            skArc(sketch, "E25.2.0.68", {"start": v(47.99, -3.9) * mm, "mid": v(47.22, -4.05) * mm, "end": v(46.57, -4.49) * mm});
            skLineSegment(sketch, "E25.2.0.69", {"start": v(55.5, 6.56) * mm, "end": v(55.5, 8.2) * mm});
            skLineSegment(sketch, "E25.2.0.70", {"start": v(44.5, -6.56) * mm, "end": v(44.5, -8.2) * mm});
            skLineSegment(sketch, "E25.2.0.71", {"start": v(56.56, -5.5) * mm, "end": v(58.2, -5.5) * mm});
            skLineSegment(sketch, "E25.2.0.72", {"start": v(55.5, -6.56) * mm, "end": v(55.5, -8.2) * mm});
            skLineSegment(sketch, "E25.2.0.73", {"start": v(40.5, 3.1) * mm, "end": v(41.8, 3.1) * mm});
            skLineSegment(sketch, "E25.2.0.74", {"start": v(53.1, 9.5) * mm, "end": v(53.1, 8.2) * mm});
            skLineSegment(sketch, "E25.2.0.75", {"start": v(46.9, -9.5) * mm, "end": v(46.9, -8.2) * mm});
            skArc(sketch, "E25.2.0.76", {"start": v(59.5, -3.4) * mm, "mid": v(59.56, -3.54) * mm, "end": v(59.7, -3.6) * mm});
            skLineSegment(sketch, "E25.2.0.77", {"start": v(60, -3.6) * mm, "end": v(59.7, -3.6) * mm});
            skLineSegment(sketch, "E25.2.0.78", {"start": v(59.5, -3.4) * mm, "end": v(59.5, -3.1) * mm});
            skArc(sketch, "E25.2.0.79", {"start": v(40.3, -3.6) * mm, "mid": v(40.44, -3.54) * mm, "end": v(40.5, -3.4) * mm});
            skArc(sketch, "E25.2.0.80", {"start": v(53.4, 9.5) * mm, "mid": v(53.54, 9.56) * mm, "end": v(53.6, 9.7) * mm});
            skLineSegment(sketch, "E25.2.0.81", {"start": v(53.1, -9.5) * mm, "end": v(53.4, -9.5) * mm});
            skArc(sketch, "E25.2.0.82", {"start": v(53.6, -9.7) * mm, "mid": v(53.54, -9.56) * mm, "end": v(53.4, -9.5) * mm});
            skLineSegment(sketch, "E25.2.0.83", {"start": v(53.6, 10) * mm, "end": v(53.6, 9.7) * mm});
            skLineSegment(sketch, "E25.2.0.84", {"start": v(40.5, -3.1) * mm, "end": v(40.5, -3.4) * mm});
            skLineSegment(sketch, "E25.2.0.85", {"start": v(53.4, 9.5) * mm, "end": v(53.1, 9.5) * mm});
            skLineSegment(sketch, "E25.2.0.86", {"start": v(40.3, -3.6) * mm, "end": v(40, -3.6) * mm});
            skLineSegment(sketch, "E25.2.0.87", {"start": v(53.6, -9.7) * mm, "end": v(53.6, -10) * mm});
            skArc(sketch, "E25.2.0.88", {"start": v(46.4, 9.7) * mm, "mid": v(46.46, 9.56) * mm, "end": v(46.6, 9.5) * mm});
            skLineSegment(sketch, "E25.2.0.89", {"start": v(46.4, -10) * mm, "end": v(46.4, -9.7) * mm});
            skLineSegment(sketch, "E25.2.0.90", {"start": v(46.6, -9.5) * mm, "end": v(46.9, -9.5) * mm});
            skLineSegment(sketch, "E25.2.0.91", {"start": v(46.4, 9.7) * mm, "end": v(46.4, 10) * mm});
            skLineSegment(sketch, "E25.2.0.92", {"start": v(46.9, 9.5) * mm, "end": v(46.6, 9.5) * mm});
            skLineSegment(sketch, "E25.2.0.93", {"start": v(40, 3.6) * mm, "end": v(40.3, 3.6) * mm});
            skArc(sketch, "E25.2.0.94", {"start": v(59.7, 3.6) * mm, "mid": v(59.56, 3.54) * mm, "end": v(59.5, 3.4) * mm});
            skArc(sketch, "E25.2.0.95", {"start": v(40.5, 3.4) * mm, "mid": v(40.44, 3.54) * mm, "end": v(40.3, 3.6) * mm});
            skLineSegment(sketch, "E25.2.0.96", {"start": v(59.7, 3.6) * mm, "end": v(60, 3.6) * mm});
            skLineSegment(sketch, "E25.2.0.97", {"start": v(40.5, 3.4) * mm, "end": v(40.5, 3.1) * mm});
            skArc(sketch, "E25.2.0.98", {"start": v(46.6, -9.5) * mm, "mid": v(46.46, -9.56) * mm, "end": v(46.4, -9.7) * mm});
            skLineSegment(sketch, "E25.2.0.99", {"start": v(59.5, 3.1) * mm, "end": v(59.5, 3.4) * mm});
            skLineSegment(sketch, "E25.direction1", {"start": v(-10, -10) * mm, "end": v(15, -10) * mm, "construction": true});
            skLineSegment(sketch, "E26.0.3.0", {"start": v(83.5, 10) * mm, "end": v(66.5, 10) * mm});
            skLineSegment(sketch, "E26.3.3.0", {"start": v(85, -8.5) * mm, "end": v(85, 8.5) * mm});
            skLineSegment(sketch, "E26.6.3.0", {"start": v(83.5, -10) * mm, "end": v(66.5, -10) * mm});
            skLineSegment(sketch, "E26.9.3.0", {"start": v(80.5, -6.56) * mm, "end": v(78.43, -4.49) * mm});
            skLineSegment(sketch, "E26.12.3.0", {"start": v(65, -8.5) * mm, "end": v(65, 8.5) * mm});
            skPoint(sketch, "E26.15.3.0", {"position": v(65, 10) * mm});
            skPoint(sketch, "E26.16.3.0", {"position": v(85, -10) * mm});
            skCircle(sketch, "E26.17.3.0", {"center": v(75, 0) * mm, "radius": 2.5 * mm});
            skLineSegment(sketch, "E26.19.3.0", {"start": v(78.1, 8.2) * mm, "end": v(80.5, 8.2) * mm});
            skPoint(sketch, "E26.22.3.0", {"position": v(71.1, -2.84) * mm});
            skPoint(sketch, "E26.23.3.0", {"position": v(78.9, 2.84) * mm});
            skLineSegment(sketch, "E26.24.3.0", {"start": v(68.44, -5.5) * mm, "end": v(70.51, -3.43) * mm});
            skLineSegment(sketch, "E26.27.3.0", {"start": v(80.5, -8.2) * mm, "end": v(78.1, -8.2) * mm});
            skPoint(sketch, "E26.30.3.0", {"position": v(65, -10) * mm});
            skLineSegment(sketch, "E26.31.3.0", {"start": v(72.99, -3.9) * mm, "end": v(77.01, -3.9) * mm});
            skLineSegment(sketch, "E26.34.3.0", {"start": v(77.01, 3.9) * mm, "end": v(72.99, 3.9) * mm});
            skLineSegment(sketch, "E26.37.3.0", {"start": v(81.56, 5.5) * mm, "end": v(79.49, 3.43) * mm});
            skPoint(sketch, "E26.40.3.0", {"position": v(65.5, 3.6) * mm});
            skPoint(sketch, "E26.41.3.0", {"position": v(84.5, -3.6) * mm});
            skLineSegment(sketch, "E26.42.3.0", {"start": v(83.2, -3.1) * mm, "end": v(83.2, -5.5) * mm});
            skLineSegment(sketch, "E26.45.3.0", {"start": v(71.57, -4.49) * mm, "end": v(69.5, -6.56) * mm});
            skPoint(sketch, "E26.48.3.0", {"position": v(65.5, -3.6) * mm});
            skPoint(sketch, "E26.49.3.0", {"position": v(84.5, 3.6) * mm});
            skLineSegment(sketch, "E26.50.3.0", {"start": v(69.5, 6.56) * mm, "end": v(71.57, 4.49) * mm});
            skLineSegment(sketch, "E26.53.3.0", {"start": v(78.9, -2.01) * mm, "end": v(78.9, 2.01) * mm});
            skLineSegment(sketch, "E26.56.3.0", {"start": v(71.1, 2.01) * mm, "end": v(71.1, -2.01) * mm});
            skLineSegment(sketch, "E26.59.3.0", {"start": v(66.8, 3.1) * mm, "end": v(66.8, 5.5) * mm});
            skPoint(sketch, "E26.62.3.0", {"position": v(85, 10) * mm});
            skPoint(sketch, "E26.63.3.0", {"position": v(78.9, -2.84) * mm});
            skPoint(sketch, "E26.64.3.0", {"position": v(71.1, 2.84) * mm});
            skPoint(sketch, "E26.65.3.0", {"position": v(75, 0) * mm});
            skPoint(sketch, "E26.66.3.0", {"position": v(78.6, -9.5) * mm});
            skPoint(sketch, "E26.67.3.0", {"position": v(72.16, 3.9) * mm});
            skPoint(sketch, "E26.68.3.0", {"position": v(71.4, 9.5) * mm});
            skLineSegment(sketch, "E26.69.3.0", {"start": v(70.51, 3.43) * mm, "end": v(68.44, 5.5) * mm});
            skPoint(sketch, "E26.72.3.0", {"position": v(77.84, -3.9) * mm});
            skPoint(sketch, "E26.73.3.0", {"position": v(78.6, 9.5) * mm});
            skLineSegment(sketch, "E26.74.3.0", {"start": v(78.43, 4.49) * mm, "end": v(80.5, 6.56) * mm});
            skLineSegment(sketch, "E26.77.3.0", {"start": v(66.8, -5.5) * mm, "end": v(66.8, -3.1) * mm});
            skPoint(sketch, "E26.80.3.0", {"position": v(77.84, 3.9) * mm});
            skLineSegment(sketch, "E26.81.3.0", {"start": v(79.49, -3.43) * mm, "end": v(81.56, -5.5) * mm});
            skLineSegment(sketch, "E26.84.3.0", {"start": v(69.5, 8.2) * mm, "end": v(71.9, 8.2) * mm});
            skLineSegment(sketch, "E26.87.3.0", {"start": v(75, 0) * mm, "end": v(75, -10) * mm, "construction": true});
            skPoint(sketch, "E26.90.3.0", {"position": v(72.16, -3.9) * mm});
            skLineSegment(sketch, "E26.91.3.0", {"start": v(83.2, 5.5) * mm, "end": v(83.2, 3.1) * mm});
            skArc(sketch, "E26.94.3.0", {"start": v(85, 8.5) * mm, "mid": v(84.56, 9.56) * mm, "end": v(83.5, 10) * mm});
            skArc(sketch, "E26.98.3.0", {"start": v(66.5, 10) * mm, "mid": v(65.44, 9.56) * mm, "end": v(65, 8.5) * mm});
            skLineSegment(sketch, "E26.102.3.0", {"start": v(71.9, -8.2) * mm, "end": v(69.5, -8.2) * mm});
            skArc(sketch, "E26.105.3.0", {"start": v(83.5, -10) * mm, "mid": v(84.56, -9.56) * mm, "end": v(85, -8.5) * mm});
            skArc(sketch, "E26.109.3.0", {"start": v(65, -8.5) * mm, "mid": v(65.44, -9.56) * mm, "end": v(66.5, -10) * mm});
            skPoint(sketch, "E26.113.3.0", {"position": v(71.4, -9.5) * mm});
            skPoint(sketch, "E26.114.3.0", {"position": v(75, 0) * mm});
            skLineSegment(sketch, "E26.115.3.0", {"start": v(78.1, -8.2) * mm, "end": v(78.1, -9.5) * mm});
            skLineSegment(sketch, "E26.118.3.0", {"start": v(66.8, -3.1) * mm, "end": v(65.5, -3.1) * mm});
            skLineSegment(sketch, "E26.121.3.0", {"start": v(68.44, -5.5) * mm, "end": v(66.8, -5.5) * mm});
            skArc(sketch, "E26.124.3.0", {"start": v(70.51, -3.43) * mm, "mid": v(70.95, -2.78) * mm, "end": v(71.1, -2.01) * mm});
            skLineSegment(sketch, "E26.128.3.0", {"start": v(71.9, 8.2) * mm, "end": v(71.9, 9.5) * mm});
            skLineSegment(sketch, "E26.131.3.0", {"start": v(83.2, 3.1) * mm, "end": v(84.5, 3.1) * mm});
            skLineSegment(sketch, "E26.134.3.0", {"start": v(81.56, 5.5) * mm, "end": v(83.2, 5.5) * mm});
            skArc(sketch, "E26.137.3.0", {"start": v(71.57, 4.49) * mm, "mid": v(72.22, 4.05) * mm, "end": v(72.99, 3.9) * mm});
            skLineSegment(sketch, "E26.141.3.0", {"start": v(69.5, 6.56) * mm, "end": v(69.5, 8.2) * mm});
            skLineSegment(sketch, "E26.144.3.0", {"start": v(84.5, -3.1) * mm, "end": v(83.2, -3.1) * mm});
            skArc(sketch, "E26.147.3.0", {"start": v(79.49, 3.43) * mm, "mid": v(79.05, 2.78) * mm, "end": v(78.9, 2.01) * mm});
            skArc(sketch, "E26.151.3.0", {"start": v(71.1, 2.01) * mm, "mid": v(70.95, 2.78) * mm, "end": v(70.51, 3.43) * mm});
            skArc(sketch, "E26.155.3.0", {"start": v(77.01, 3.9) * mm, "mid": v(77.78, 4.05) * mm, "end": v(78.43, 4.49) * mm});
            skArc(sketch, "E26.159.3.0", {"start": v(78.43, -4.49) * mm, "mid": v(77.78, -4.05) * mm, "end": v(77.01, -3.9) * mm});
            skArc(sketch, "E26.163.3.0", {"start": v(78.9, -2.01) * mm, "mid": v(79.05, -2.78) * mm, "end": v(79.49, -3.43) * mm});
            skLineSegment(sketch, "E26.167.3.0", {"start": v(68.44, 5.5) * mm, "end": v(66.8, 5.5) * mm});
            skArc(sketch, "E26.170.3.0", {"start": v(72.99, -3.9) * mm, "mid": v(72.22, -4.05) * mm, "end": v(71.57, -4.49) * mm});
            skLineSegment(sketch, "E26.174.3.0", {"start": v(80.5, 6.56) * mm, "end": v(80.5, 8.2) * mm});
            skLineSegment(sketch, "E26.177.3.0", {"start": v(69.5, -6.56) * mm, "end": v(69.5, -8.2) * mm});
            skLineSegment(sketch, "E26.180.3.0", {"start": v(81.56, -5.5) * mm, "end": v(83.2, -5.5) * mm});
            skLineSegment(sketch, "E26.183.3.0", {"start": v(80.5, -6.56) * mm, "end": v(80.5, -8.2) * mm});
            skLineSegment(sketch, "E26.186.3.0", {"start": v(65.5, 3.1) * mm, "end": v(66.8, 3.1) * mm});
            skLineSegment(sketch, "E26.189.3.0", {"start": v(78.1, 9.5) * mm, "end": v(78.1, 8.2) * mm});
            skLineSegment(sketch, "E26.192.3.0", {"start": v(71.9, -9.5) * mm, "end": v(71.9, -8.2) * mm});
            skArc(sketch, "E26.195.3.0", {"start": v(84.5, -3.4) * mm, "mid": v(84.56, -3.54) * mm, "end": v(84.7, -3.6) * mm});
            skLineSegment(sketch, "E26.199.3.0", {"start": v(85, -3.6) * mm, "end": v(84.7, -3.6) * mm});
            skLineSegment(sketch, "E26.202.3.0", {"start": v(84.5, -3.4) * mm, "end": v(84.5, -3.1) * mm});
            skArc(sketch, "E26.205.3.0", {"start": v(65.3, -3.6) * mm, "mid": v(65.44, -3.54) * mm, "end": v(65.5, -3.4) * mm});
            skArc(sketch, "E26.209.3.0", {"start": v(78.4, 9.5) * mm, "mid": v(78.54, 9.56) * mm, "end": v(78.6, 9.7) * mm});
            skLineSegment(sketch, "E26.213.3.0", {"start": v(78.1, -9.5) * mm, "end": v(78.4, -9.5) * mm});
            skArc(sketch, "E26.216.3.0", {"start": v(78.6, -9.7) * mm, "mid": v(78.54, -9.56) * mm, "end": v(78.4, -9.5) * mm});
            skLineSegment(sketch, "E26.220.3.0", {"start": v(78.6, 10) * mm, "end": v(78.6, 9.7) * mm});
            skLineSegment(sketch, "E26.223.3.0", {"start": v(65.5, -3.1) * mm, "end": v(65.5, -3.4) * mm});
            skLineSegment(sketch, "E26.226.3.0", {"start": v(78.4, 9.5) * mm, "end": v(78.1, 9.5) * mm});
            skLineSegment(sketch, "E26.229.3.0", {"start": v(65.3, -3.6) * mm, "end": v(65, -3.6) * mm});
            skLineSegment(sketch, "E26.232.3.0", {"start": v(78.6, -9.7) * mm, "end": v(78.6, -10) * mm});
            skArc(sketch, "E26.235.3.0", {"start": v(71.4, 9.7) * mm, "mid": v(71.46, 9.56) * mm, "end": v(71.6, 9.5) * mm});
            skLineSegment(sketch, "E26.239.3.0", {"start": v(71.4, -10) * mm, "end": v(71.4, -9.7) * mm});
            skLineSegment(sketch, "E26.242.3.0", {"start": v(71.6, -9.5) * mm, "end": v(71.9, -9.5) * mm});
            skLineSegment(sketch, "E26.245.3.0", {"start": v(71.4, 9.7) * mm, "end": v(71.4, 10) * mm});
            skLineSegment(sketch, "E26.248.3.0", {"start": v(71.9, 9.5) * mm, "end": v(71.6, 9.5) * mm});
            skLineSegment(sketch, "E26.251.3.0", {"start": v(65, 3.6) * mm, "end": v(65.3, 3.6) * mm});
            skArc(sketch, "E26.254.3.0", {"start": v(84.7, 3.6) * mm, "mid": v(84.56, 3.54) * mm, "end": v(84.5, 3.4) * mm});
            skArc(sketch, "E26.258.3.0", {"start": v(65.5, 3.4) * mm, "mid": v(65.44, 3.54) * mm, "end": v(65.3, 3.6) * mm});
            skLineSegment(sketch, "E26.262.3.0", {"start": v(84.7, 3.6) * mm, "end": v(85, 3.6) * mm});
            skLineSegment(sketch, "E26.265.3.0", {"start": v(65.5, 3.4) * mm, "end": v(65.5, 3.1) * mm});
            skArc(sketch, "E26.268.3.0", {"start": v(71.6, -9.5) * mm, "mid": v(71.46, -9.56) * mm, "end": v(71.4, -9.7) * mm});
            skLineSegment(sketch, "E26.272.3.0", {"start": v(84.5, 3.1) * mm, "end": v(84.5, 3.4) * mm});
            skLineSegment(sketch, "E27.0.4.0", {"start": v(108.5, 10) * mm, "end": v(91.5, 10) * mm});
            skLineSegment(sketch, "E27.3.4.0", {"start": v(110, -8.5) * mm, "end": v(110, 8.5) * mm});
            skLineSegment(sketch, "E27.6.4.0", {"start": v(108.5, -10) * mm, "end": v(91.5, -10) * mm});
            skLineSegment(sketch, "E27.9.4.0", {"start": v(105.5, -6.56) * mm, "end": v(103.43, -4.49) * mm});
            skLineSegment(sketch, "E27.12.4.0", {"start": v(90, -8.5) * mm, "end": v(90, 8.5) * mm});
            skPoint(sketch, "E27.15.4.0", {"position": v(90, 10) * mm});
            skPoint(sketch, "E27.16.4.0", {"position": v(110, -10) * mm});
            skCircle(sketch, "E27.17.4.0", {"center": v(100, 0) * mm, "radius": 2.5 * mm});
            skLineSegment(sketch, "E27.19.4.0", {"start": v(103.1, 8.2) * mm, "end": v(105.5, 8.2) * mm});
            skPoint(sketch, "E27.22.4.0", {"position": v(96.1, -2.84) * mm});
            skPoint(sketch, "E27.23.4.0", {"position": v(103.9, 2.84) * mm});
            skLineSegment(sketch, "E27.24.4.0", {"start": v(93.44, -5.5) * mm, "end": v(95.51, -3.43) * mm});
            skLineSegment(sketch, "E27.27.4.0", {"start": v(105.5, -8.2) * mm, "end": v(103.1, -8.2) * mm});
            skPoint(sketch, "E27.30.4.0", {"position": v(90, -10) * mm});
            skLineSegment(sketch, "E27.31.4.0", {"start": v(97.99, -3.9) * mm, "end": v(102.01, -3.9) * mm});
            skLineSegment(sketch, "E27.34.4.0", {"start": v(102.01, 3.9) * mm, "end": v(97.99, 3.9) * mm});
            skLineSegment(sketch, "E27.37.4.0", {"start": v(106.56, 5.5) * mm, "end": v(104.49, 3.43) * mm});
            skPoint(sketch, "E27.40.4.0", {"position": v(90.5, 3.6) * mm});
            skPoint(sketch, "E27.41.4.0", {"position": v(109.5, -3.6) * mm});
            skLineSegment(sketch, "E27.42.4.0", {"start": v(108.2, -3.1) * mm, "end": v(108.2, -5.5) * mm});
            skLineSegment(sketch, "E27.45.4.0", {"start": v(96.57, -4.49) * mm, "end": v(94.5, -6.56) * mm});
            skPoint(sketch, "E27.48.4.0", {"position": v(90.5, -3.6) * mm});
            skPoint(sketch, "E27.49.4.0", {"position": v(109.5, 3.6) * mm});
            skLineSegment(sketch, "E27.50.4.0", {"start": v(94.5, 6.56) * mm, "end": v(96.57, 4.49) * mm});
            skLineSegment(sketch, "E27.53.4.0", {"start": v(103.9, -2.01) * mm, "end": v(103.9, 2.01) * mm});
            skLineSegment(sketch, "E27.56.4.0", {"start": v(96.1, 2.01) * mm, "end": v(96.1, -2.01) * mm});
            skLineSegment(sketch, "E27.59.4.0", {"start": v(91.8, 3.1) * mm, "end": v(91.8, 5.5) * mm});
            skPoint(sketch, "E27.62.4.0", {"position": v(110, 10) * mm});
            skPoint(sketch, "E27.63.4.0", {"position": v(103.9, -2.84) * mm});
            skPoint(sketch, "E27.64.4.0", {"position": v(96.1, 2.84) * mm});
            skPoint(sketch, "E27.65.4.0", {"position": v(100, 0) * mm});
            skPoint(sketch, "E27.66.4.0", {"position": v(103.6, -9.5) * mm});
            skPoint(sketch, "E27.67.4.0", {"position": v(97.16, 3.9) * mm});
            skPoint(sketch, "E27.68.4.0", {"position": v(96.4, 9.5) * mm});
            skLineSegment(sketch, "E27.69.4.0", {"start": v(95.51, 3.43) * mm, "end": v(93.44, 5.5) * mm});
            skPoint(sketch, "E27.72.4.0", {"position": v(102.84, -3.9) * mm});
            skPoint(sketch, "E27.73.4.0", {"position": v(103.6, 9.5) * mm});
            skLineSegment(sketch, "E27.74.4.0", {"start": v(103.43, 4.49) * mm, "end": v(105.5, 6.56) * mm});
            skLineSegment(sketch, "E27.77.4.0", {"start": v(91.8, -5.5) * mm, "end": v(91.8, -3.1) * mm});
            skPoint(sketch, "E27.80.4.0", {"position": v(102.84, 3.9) * mm});
            skLineSegment(sketch, "E27.81.4.0", {"start": v(104.49, -3.43) * mm, "end": v(106.56, -5.5) * mm});
            skLineSegment(sketch, "E27.84.4.0", {"start": v(94.5, 8.2) * mm, "end": v(96.9, 8.2) * mm});
            skLineSegment(sketch, "E27.87.4.0", {"start": v(100, 0) * mm, "end": v(100, -10) * mm, "construction": true});
            skPoint(sketch, "E27.90.4.0", {"position": v(97.16, -3.9) * mm});
            skLineSegment(sketch, "E27.91.4.0", {"start": v(108.2, 5.5) * mm, "end": v(108.2, 3.1) * mm});
            skArc(sketch, "E27.94.4.0", {"start": v(110, 8.5) * mm, "mid": v(109.56, 9.56) * mm, "end": v(108.5, 10) * mm});
            skArc(sketch, "E27.98.4.0", {"start": v(91.5, 10) * mm, "mid": v(90.44, 9.56) * mm, "end": v(90, 8.5) * mm});
            skLineSegment(sketch, "E27.102.4.0", {"start": v(96.9, -8.2) * mm, "end": v(94.5, -8.2) * mm});
            skArc(sketch, "E27.105.4.0", {"start": v(108.5, -10) * mm, "mid": v(109.56, -9.56) * mm, "end": v(110, -8.5) * mm});
            skArc(sketch, "E27.109.4.0", {"start": v(90, -8.5) * mm, "mid": v(90.44, -9.56) * mm, "end": v(91.5, -10) * mm});
            skPoint(sketch, "E27.113.4.0", {"position": v(96.4, -9.5) * mm});
            skPoint(sketch, "E27.114.4.0", {"position": v(100, 0) * mm});
            skLineSegment(sketch, "E27.115.4.0", {"start": v(103.1, -8.2) * mm, "end": v(103.1, -9.5) * mm});
            skLineSegment(sketch, "E27.118.4.0", {"start": v(91.8, -3.1) * mm, "end": v(90.5, -3.1) * mm});
            skLineSegment(sketch, "E27.121.4.0", {"start": v(93.44, -5.5) * mm, "end": v(91.8, -5.5) * mm});
            skArc(sketch, "E27.124.4.0", {"start": v(95.51, -3.43) * mm, "mid": v(95.95, -2.78) * mm, "end": v(96.1, -2.01) * mm});
            skLineSegment(sketch, "E27.128.4.0", {"start": v(96.9, 8.2) * mm, "end": v(96.9, 9.5) * mm});
            skLineSegment(sketch, "E27.131.4.0", {"start": v(108.2, 3.1) * mm, "end": v(109.5, 3.1) * mm});
            skLineSegment(sketch, "E27.134.4.0", {"start": v(106.56, 5.5) * mm, "end": v(108.2, 5.5) * mm});
            skArc(sketch, "E27.137.4.0", {"start": v(96.57, 4.49) * mm, "mid": v(97.22, 4.05) * mm, "end": v(97.99, 3.9) * mm});
            skLineSegment(sketch, "E27.141.4.0", {"start": v(94.5, 6.56) * mm, "end": v(94.5, 8.2) * mm});
            skLineSegment(sketch, "E27.144.4.0", {"start": v(109.5, -3.1) * mm, "end": v(108.2, -3.1) * mm});
            skArc(sketch, "E27.147.4.0", {"start": v(104.49, 3.43) * mm, "mid": v(104.05, 2.78) * mm, "end": v(103.9, 2.01) * mm});
            skArc(sketch, "E27.151.4.0", {"start": v(96.1, 2.01) * mm, "mid": v(95.95, 2.78) * mm, "end": v(95.51, 3.43) * mm});
            skArc(sketch, "E27.155.4.0", {"start": v(102.01, 3.9) * mm, "mid": v(102.78, 4.05) * mm, "end": v(103.43, 4.49) * mm});
            skArc(sketch, "E27.159.4.0", {"start": v(103.43, -4.49) * mm, "mid": v(102.78, -4.05) * mm, "end": v(102.01, -3.9) * mm});
            skArc(sketch, "E27.163.4.0", {"start": v(103.9, -2.01) * mm, "mid": v(104.05, -2.78) * mm, "end": v(104.49, -3.43) * mm});
            skLineSegment(sketch, "E27.167.4.0", {"start": v(93.44, 5.5) * mm, "end": v(91.8, 5.5) * mm});
            skArc(sketch, "E27.170.4.0", {"start": v(97.99, -3.9) * mm, "mid": v(97.22, -4.05) * mm, "end": v(96.57, -4.49) * mm});
            skLineSegment(sketch, "E27.174.4.0", {"start": v(105.5, 6.56) * mm, "end": v(105.5, 8.2) * mm});
            skLineSegment(sketch, "E27.177.4.0", {"start": v(94.5, -6.56) * mm, "end": v(94.5, -8.2) * mm});
            skLineSegment(sketch, "E27.180.4.0", {"start": v(106.56, -5.5) * mm, "end": v(108.2, -5.5) * mm});
            skLineSegment(sketch, "E27.183.4.0", {"start": v(105.5, -6.56) * mm, "end": v(105.5, -8.2) * mm});
            skLineSegment(sketch, "E27.186.4.0", {"start": v(90.5, 3.1) * mm, "end": v(91.8, 3.1) * mm});
            skLineSegment(sketch, "E27.189.4.0", {"start": v(103.1, 9.5) * mm, "end": v(103.1, 8.2) * mm});
            skLineSegment(sketch, "E27.192.4.0", {"start": v(96.9, -9.5) * mm, "end": v(96.9, -8.2) * mm});
            skArc(sketch, "E27.195.4.0", {"start": v(109.5, -3.4) * mm, "mid": v(109.56, -3.54) * mm, "end": v(109.7, -3.6) * mm});
            skLineSegment(sketch, "E27.199.4.0", {"start": v(110, -3.6) * mm, "end": v(109.7, -3.6) * mm});
            skLineSegment(sketch, "E27.202.4.0", {"start": v(109.5, -3.4) * mm, "end": v(109.5, -3.1) * mm});
            skArc(sketch, "E27.205.4.0", {"start": v(90.3, -3.6) * mm, "mid": v(90.44, -3.54) * mm, "end": v(90.5, -3.4) * mm});
            skArc(sketch, "E27.209.4.0", {"start": v(103.4, 9.5) * mm, "mid": v(103.54, 9.56) * mm, "end": v(103.6, 9.7) * mm});
            skLineSegment(sketch, "E27.213.4.0", {"start": v(103.1, -9.5) * mm, "end": v(103.4, -9.5) * mm});
            skArc(sketch, "E27.216.4.0", {"start": v(103.6, -9.7) * mm, "mid": v(103.54, -9.56) * mm, "end": v(103.4, -9.5) * mm});
            skLineSegment(sketch, "E27.220.4.0", {"start": v(103.6, 10) * mm, "end": v(103.6, 9.7) * mm});
            skLineSegment(sketch, "E27.223.4.0", {"start": v(90.5, -3.1) * mm, "end": v(90.5, -3.4) * mm});
            skLineSegment(sketch, "E27.226.4.0", {"start": v(103.4, 9.5) * mm, "end": v(103.1, 9.5) * mm});
            skLineSegment(sketch, "E27.229.4.0", {"start": v(90.3, -3.6) * mm, "end": v(90, -3.6) * mm});
            skLineSegment(sketch, "E27.232.4.0", {"start": v(103.6, -9.7) * mm, "end": v(103.6, -10) * mm});
            skArc(sketch, "E27.235.4.0", {"start": v(96.4, 9.7) * mm, "mid": v(96.46, 9.56) * mm, "end": v(96.6, 9.5) * mm});
            skLineSegment(sketch, "E27.239.4.0", {"start": v(96.4, -10) * mm, "end": v(96.4, -9.7) * mm});
            skLineSegment(sketch, "E27.242.4.0", {"start": v(96.6, -9.5) * mm, "end": v(96.9, -9.5) * mm});
            skLineSegment(sketch, "E27.245.4.0", {"start": v(96.4, 9.7) * mm, "end": v(96.4, 10) * mm});
            skLineSegment(sketch, "E27.248.4.0", {"start": v(96.9, 9.5) * mm, "end": v(96.6, 9.5) * mm});
            skLineSegment(sketch, "E27.251.4.0", {"start": v(90, 3.6) * mm, "end": v(90.3, 3.6) * mm});
            skArc(sketch, "E27.254.4.0", {"start": v(109.7, 3.6) * mm, "mid": v(109.56, 3.54) * mm, "end": v(109.5, 3.4) * mm});
            skArc(sketch, "E27.258.4.0", {"start": v(90.5, 3.4) * mm, "mid": v(90.44, 3.54) * mm, "end": v(90.3, 3.6) * mm});
            skLineSegment(sketch, "E27.262.4.0", {"start": v(109.7, 3.6) * mm, "end": v(110, 3.6) * mm});
            skLineSegment(sketch, "E27.265.4.0", {"start": v(90.5, 3.4) * mm, "end": v(90.5, 3.1) * mm});
            skArc(sketch, "E27.268.4.0", {"start": v(96.6, -9.5) * mm, "mid": v(96.46, -9.56) * mm, "end": v(96.4, -9.7) * mm});
            skLineSegment(sketch, "E27.272.4.0", {"start": v(109.5, 3.1) * mm, "end": v(109.5, 3.4) * mm});
            skLineSegment(sketch, "E27.0.5.0", {"start": v(133.5, 10) * mm, "end": v(116.5, 10) * mm});
            skLineSegment(sketch, "E27.3.5.0", {"start": v(135, -8.5) * mm, "end": v(135, 8.5) * mm});
            skLineSegment(sketch, "E27.6.5.0", {"start": v(133.5, -10) * mm, "end": v(116.5, -10) * mm});
            skLineSegment(sketch, "E27.9.5.0", {"start": v(130.5, -6.56) * mm, "end": v(128.43, -4.49) * mm});
            skLineSegment(sketch, "E27.12.5.0", {"start": v(115, -8.5) * mm, "end": v(115, 8.5) * mm});
            skPoint(sketch, "E27.15.5.0", {"position": v(115, 10) * mm});
            skPoint(sketch, "E27.16.5.0", {"position": v(135, -10) * mm});
            skCircle(sketch, "E27.17.5.0", {"center": v(125, 0) * mm, "radius": 2.5 * mm});
            skLineSegment(sketch, "E27.19.5.0", {"start": v(128.1, 8.2) * mm, "end": v(130.5, 8.2) * mm});
            skPoint(sketch, "E27.22.5.0", {"position": v(121.1, -2.84) * mm});
            skPoint(sketch, "E27.23.5.0", {"position": v(128.9, 2.84) * mm});
            skLineSegment(sketch, "E27.24.5.0", {"start": v(118.44, -5.5) * mm, "end": v(120.51, -3.43) * mm});
            skLineSegment(sketch, "E27.27.5.0", {"start": v(130.5, -8.2) * mm, "end": v(128.1, -8.2) * mm});
            skPoint(sketch, "E27.30.5.0", {"position": v(115, -10) * mm});
            skLineSegment(sketch, "E27.31.5.0", {"start": v(122.99, -3.9) * mm, "end": v(127.01, -3.9) * mm});
            skLineSegment(sketch, "E27.34.5.0", {"start": v(127.01, 3.9) * mm, "end": v(122.99, 3.9) * mm});
            skLineSegment(sketch, "E27.37.5.0", {"start": v(131.56, 5.5) * mm, "end": v(129.49, 3.43) * mm});
            skPoint(sketch, "E27.40.5.0", {"position": v(115.5, 3.6) * mm});
            skPoint(sketch, "E27.41.5.0", {"position": v(134.5, -3.6) * mm});
            skLineSegment(sketch, "E27.42.5.0", {"start": v(133.2, -3.1) * mm, "end": v(133.2, -5.5) * mm});
            skLineSegment(sketch, "E27.45.5.0", {"start": v(121.57, -4.49) * mm, "end": v(119.5, -6.56) * mm});
            skPoint(sketch, "E27.48.5.0", {"position": v(115.5, -3.6) * mm});
            skPoint(sketch, "E27.49.5.0", {"position": v(134.5, 3.6) * mm});
            skLineSegment(sketch, "E27.50.5.0", {"start": v(119.5, 6.56) * mm, "end": v(121.57, 4.49) * mm});
            skLineSegment(sketch, "E27.53.5.0", {"start": v(128.9, -2.01) * mm, "end": v(128.9, 2.01) * mm});
            skLineSegment(sketch, "E27.56.5.0", {"start": v(121.1, 2.01) * mm, "end": v(121.1, -2.01) * mm});
            skLineSegment(sketch, "E27.59.5.0", {"start": v(116.8, 3.1) * mm, "end": v(116.8, 5.5) * mm});
            skPoint(sketch, "E27.62.5.0", {"position": v(135, 10) * mm});
            skPoint(sketch, "E27.63.5.0", {"position": v(128.9, -2.84) * mm});
            skPoint(sketch, "E27.64.5.0", {"position": v(121.1, 2.84) * mm});
            skPoint(sketch, "E27.65.5.0", {"position": v(125, 0) * mm});
            skPoint(sketch, "E27.66.5.0", {"position": v(128.6, -9.5) * mm});
            skPoint(sketch, "E27.67.5.0", {"position": v(122.16, 3.9) * mm});
            skPoint(sketch, "E27.68.5.0", {"position": v(121.4, 9.5) * mm});
            skLineSegment(sketch, "E27.69.5.0", {"start": v(120.51, 3.43) * mm, "end": v(118.44, 5.5) * mm});
            skPoint(sketch, "E27.72.5.0", {"position": v(127.84, -3.9) * mm});
            skPoint(sketch, "E27.73.5.0", {"position": v(128.6, 9.5) * mm});
            skLineSegment(sketch, "E27.74.5.0", {"start": v(128.43, 4.49) * mm, "end": v(130.5, 6.56) * mm});
            skLineSegment(sketch, "E27.77.5.0", {"start": v(116.8, -5.5) * mm, "end": v(116.8, -3.1) * mm});
            skPoint(sketch, "E27.80.5.0", {"position": v(127.84, 3.9) * mm});
            skLineSegment(sketch, "E27.81.5.0", {"start": v(129.49, -3.43) * mm, "end": v(131.56, -5.5) * mm});
            skLineSegment(sketch, "E27.84.5.0", {"start": v(119.5, 8.2) * mm, "end": v(121.9, 8.2) * mm});
            skLineSegment(sketch, "E27.87.5.0", {"start": v(125, 0) * mm, "end": v(125, -10) * mm, "construction": true});
            skPoint(sketch, "E27.90.5.0", {"position": v(122.16, -3.9) * mm});
            skLineSegment(sketch, "E27.91.5.0", {"start": v(133.2, 5.5) * mm, "end": v(133.2, 3.1) * mm});
            skArc(sketch, "E27.94.5.0", {"start": v(135, 8.5) * mm, "mid": v(134.56, 9.56) * mm, "end": v(133.5, 10) * mm});
            skArc(sketch, "E27.98.5.0", {"start": v(116.5, 10) * mm, "mid": v(115.44, 9.56) * mm, "end": v(115, 8.5) * mm});
            skLineSegment(sketch, "E27.102.5.0", {"start": v(121.9, -8.2) * mm, "end": v(119.5, -8.2) * mm});
            skArc(sketch, "E27.105.5.0", {"start": v(133.5, -10) * mm, "mid": v(134.56, -9.56) * mm, "end": v(135, -8.5) * mm});
            skArc(sketch, "E27.109.5.0", {"start": v(115, -8.5) * mm, "mid": v(115.44, -9.56) * mm, "end": v(116.5, -10) * mm});
            skPoint(sketch, "E27.113.5.0", {"position": v(121.4, -9.5) * mm});
            skPoint(sketch, "E27.114.5.0", {"position": v(125, 0) * mm});
            skLineSegment(sketch, "E27.115.5.0", {"start": v(128.1, -8.2) * mm, "end": v(128.1, -9.5) * mm});
            skLineSegment(sketch, "E27.118.5.0", {"start": v(116.8, -3.1) * mm, "end": v(115.5, -3.1) * mm});
            skLineSegment(sketch, "E27.121.5.0", {"start": v(118.44, -5.5) * mm, "end": v(116.8, -5.5) * mm});
            skArc(sketch, "E27.124.5.0", {"start": v(120.51, -3.43) * mm, "mid": v(120.95, -2.78) * mm, "end": v(121.1, -2.01) * mm});
            skLineSegment(sketch, "E27.128.5.0", {"start": v(121.9, 8.2) * mm, "end": v(121.9, 9.5) * mm});
            skLineSegment(sketch, "E27.131.5.0", {"start": v(133.2, 3.1) * mm, "end": v(134.5, 3.1) * mm});
            skLineSegment(sketch, "E27.134.5.0", {"start": v(131.56, 5.5) * mm, "end": v(133.2, 5.5) * mm});
            skArc(sketch, "E27.137.5.0", {"start": v(121.57, 4.49) * mm, "mid": v(122.22, 4.05) * mm, "end": v(122.99, 3.9) * mm});
            skLineSegment(sketch, "E27.141.5.0", {"start": v(119.5, 6.56) * mm, "end": v(119.5, 8.2) * mm});
            skLineSegment(sketch, "E27.144.5.0", {"start": v(134.5, -3.1) * mm, "end": v(133.2, -3.1) * mm});
            skArc(sketch, "E27.147.5.0", {"start": v(129.49, 3.43) * mm, "mid": v(129.05, 2.78) * mm, "end": v(128.9, 2.01) * mm});
            skArc(sketch, "E27.151.5.0", {"start": v(121.1, 2.01) * mm, "mid": v(120.95, 2.78) * mm, "end": v(120.51, 3.43) * mm});
            skArc(sketch, "E27.155.5.0", {"start": v(127.01, 3.9) * mm, "mid": v(127.78, 4.05) * mm, "end": v(128.43, 4.49) * mm});
            skArc(sketch, "E27.159.5.0", {"start": v(128.43, -4.49) * mm, "mid": v(127.78, -4.05) * mm, "end": v(127.01, -3.9) * mm});
            skArc(sketch, "E27.163.5.0", {"start": v(128.9, -2.01) * mm, "mid": v(129.05, -2.78) * mm, "end": v(129.49, -3.43) * mm});
            skLineSegment(sketch, "E27.167.5.0", {"start": v(118.44, 5.5) * mm, "end": v(116.8, 5.5) * mm});
            skArc(sketch, "E27.170.5.0", {"start": v(122.99, -3.9) * mm, "mid": v(122.22, -4.05) * mm, "end": v(121.57, -4.49) * mm});
            skLineSegment(sketch, "E27.174.5.0", {"start": v(130.5, 6.56) * mm, "end": v(130.5, 8.2) * mm});
            skLineSegment(sketch, "E27.177.5.0", {"start": v(119.5, -6.56) * mm, "end": v(119.5, -8.2) * mm});
            skLineSegment(sketch, "E27.180.5.0", {"start": v(131.56, -5.5) * mm, "end": v(133.2, -5.5) * mm});
            skLineSegment(sketch, "E27.183.5.0", {"start": v(130.5, -6.56) * mm, "end": v(130.5, -8.2) * mm});
            skLineSegment(sketch, "E27.186.5.0", {"start": v(115.5, 3.1) * mm, "end": v(116.8, 3.1) * mm});
            skLineSegment(sketch, "E27.189.5.0", {"start": v(128.1, 9.5) * mm, "end": v(128.1, 8.2) * mm});
            skLineSegment(sketch, "E27.192.5.0", {"start": v(121.9, -9.5) * mm, "end": v(121.9, -8.2) * mm});
            skArc(sketch, "E27.195.5.0", {"start": v(134.5, -3.4) * mm, "mid": v(134.56, -3.54) * mm, "end": v(134.7, -3.6) * mm});
            skLineSegment(sketch, "E27.199.5.0", {"start": v(135, -3.6) * mm, "end": v(134.7, -3.6) * mm});
            skLineSegment(sketch, "E27.202.5.0", {"start": v(134.5, -3.4) * mm, "end": v(134.5, -3.1) * mm});
            skArc(sketch, "E27.205.5.0", {"start": v(115.3, -3.6) * mm, "mid": v(115.44, -3.54) * mm, "end": v(115.5, -3.4) * mm});
            skArc(sketch, "E27.209.5.0", {"start": v(128.4, 9.5) * mm, "mid": v(128.54, 9.56) * mm, "end": v(128.6, 9.7) * mm});
            skLineSegment(sketch, "E27.213.5.0", {"start": v(128.1, -9.5) * mm, "end": v(128.4, -9.5) * mm});
            skArc(sketch, "E27.216.5.0", {"start": v(128.6, -9.7) * mm, "mid": v(128.54, -9.56) * mm, "end": v(128.4, -9.5) * mm});
            skLineSegment(sketch, "E27.220.5.0", {"start": v(128.6, 10) * mm, "end": v(128.6, 9.7) * mm});
            skLineSegment(sketch, "E27.223.5.0", {"start": v(115.5, -3.1) * mm, "end": v(115.5, -3.4) * mm});
            skLineSegment(sketch, "E27.226.5.0", {"start": v(128.4, 9.5) * mm, "end": v(128.1, 9.5) * mm});
            skLineSegment(sketch, "E27.229.5.0", {"start": v(115.3, -3.6) * mm, "end": v(115, -3.6) * mm});
            skLineSegment(sketch, "E27.232.5.0", {"start": v(128.6, -9.7) * mm, "end": v(128.6, -10) * mm});
            skArc(sketch, "E27.235.5.0", {"start": v(121.4, 9.7) * mm, "mid": v(121.46, 9.56) * mm, "end": v(121.6, 9.5) * mm});
            skLineSegment(sketch, "E27.239.5.0", {"start": v(121.4, -10) * mm, "end": v(121.4, -9.7) * mm});
            skLineSegment(sketch, "E27.242.5.0", {"start": v(121.6, -9.5) * mm, "end": v(121.9, -9.5) * mm});
            skLineSegment(sketch, "E27.245.5.0", {"start": v(121.4, 9.7) * mm, "end": v(121.4, 10) * mm});
            skLineSegment(sketch, "E27.248.5.0", {"start": v(121.9, 9.5) * mm, "end": v(121.6, 9.5) * mm});
            skLineSegment(sketch, "E27.251.5.0", {"start": v(115, 3.6) * mm, "end": v(115.3, 3.6) * mm});
            skArc(sketch, "E27.254.5.0", {"start": v(134.7, 3.6) * mm, "mid": v(134.56, 3.54) * mm, "end": v(134.5, 3.4) * mm});
            skArc(sketch, "E27.258.5.0", {"start": v(115.5, 3.4) * mm, "mid": v(115.44, 3.54) * mm, "end": v(115.3, 3.6) * mm});
            skLineSegment(sketch, "E27.262.5.0", {"start": v(134.7, 3.6) * mm, "end": v(135, 3.6) * mm});
            skLineSegment(sketch, "E27.265.5.0", {"start": v(115.5, 3.4) * mm, "end": v(115.5, 3.1) * mm});
            skArc(sketch, "E27.268.5.0", {"start": v(121.6, -9.5) * mm, "mid": v(121.46, -9.56) * mm, "end": v(121.4, -9.7) * mm});
            skLineSegment(sketch, "E27.272.5.0", {"start": v(134.5, 3.1) * mm, "end": v(134.5, 3.4) * mm});
            skSolve(sketch);
        }
        {
            var Q0;
            {var subQ3=sQuery(id+"F3.wireOp",EDGE,"E1.filletArc");Q0=makeQuery(id+"F3.imprint","IMPRINT",FACE,{"disambiguationData":[TD([[makeQuery(id+"F3.imprint","IMPRINT",EDGE,{"derivedFrom":subQ3}),1.0]])]});}
            extrude(context, id + "F4", {"entities" : qUnion([Q0]), "depth" : (getVariable(context, 'X')) * mm, "offsetDistance" : 25 * mm});
        }
        {
            var Q0;
            Q0=makeQuery(id+"F3.imprint","IMPRINT",FACE,{"disambiguationData":[TD([[makeQuery(id+"F3.imprint","IMPRINT",EDGE,{"derivedFrom":sQuery(id+"F3.wireOp",EDGE,"E25.1.0.3")}),-1.0]])]});
            extrude(context, id + "F5", {"entities" : qUnion([Q0]), "depth" : (getVariable(context, 'Y')) * mm, "offsetDistance" : 25 * mm});
        }
        {
            var Q0;
            Q0=makeQuery(id+"F3.imprint","IMPRINT",FACE,{"disambiguationData":[TD([[makeQuery(id+"F3.imprint","IMPRINT",EDGE,{"derivedFrom":sQuery(id+"F3.wireOp",EDGE,"E25.2.0.3")}),-1.0]])]});
            extrude(context, id + "F6", {"entities" : qUnion([Q0]), "depth" : (getVariable(context, 'Y') + 20 * 2) * mm, "offsetDistance" : 25 * mm});
        }
        {
            var Q0;
            Q0=makeQuery(id+"F3.imprint","IMPRINT",FACE,{"disambiguationData":[TD([[makeQuery(id+"F3.imprint","IMPRINT",EDGE,{"derivedFrom":sQuery(id+"F3.wireOp",EDGE,"E26.9.3.0")}),-1.0]])]});
            extrude(context, id + "F7", {"entities" : qUnion([Q0]), "depth" : getVariable(context, 'Z') * mm, "offsetDistance" : 25 * mm});
        }
        {
            var Q0;
            Q0=qCreatedBy(makeId("Top.planeOp"),FACE);
            var sketch = newSketch(context, id + "F8", { "sketchPlane" : qUnion([Q0])});
            skCircle(sketch, "E28", {"center": v(0, -50) * mm, "radius": 4 * mm});
            skCircle(sketch, "E29.1.0.0", {"center": v(25, -50) * mm, "radius": 4 * mm});
            skCircle(sketch, "E29.2.0.0", {"center": v(50, -50) * mm, "radius": 4 * mm});
            skLineSegment(sketch, "E29.direction1", {"start": v(0, -50) * mm, "end": v(25, -50) * mm, "construction": true});
            skSolve(sketch);
        }
        {
            var Q0;
            Q0=makeQuery(id+"F8.imprint","IMPRINT",FACE,{"disambiguationData":[TD([[makeQuery(id+"F8.imprint","IMPRINT",EDGE,{"derivedFrom":sQuery(id+"F8.wireOp",EDGE,"E28")}),1.0]])]});
            extrude(context, id + "F9", {"entities" : qUnion([Q0]), "depth" : 400 * mm, "offsetDistance" : 25 * mm});
        }
        {
            var Q0;
            Q0=makeQuery(id+"F8.imprint","IMPRINT",FACE,{"disambiguationData":[TD([[makeQuery(id+"F8.imprint","IMPRINT",EDGE,{"derivedFrom":sQuery(id+"F8.wireOp",EDGE,"E29.1.0.0")}),1.0]])]});
            extrude(context, id + "F10", {"entities" : qUnion([Q0]), "depth" : 300 * mm, "offsetDistance" : 25 * mm});
        }
        {
            var Q0;
            Q0=makeQuery(id+"F8.imprint","IMPRINT",FACE,{"disambiguationData":[TD([[makeQuery(id+"F8.imprint","IMPRINT",EDGE,{"derivedFrom":sQuery(id+"F8.wireOp",EDGE,"E29.2.0.0")}),1.0]])]});
            extrude(context, id + "F11", {"entities" : qUnion([Q0]), "depth" : 400 * mm, "offsetDistance" : 25 * mm});
        }
        {
            var Q0;
            Q0=qCreatedBy(makeId("Top.planeOp"),FACE);
            var sketch = newSketch(context, id + "F12", { "sketchPlane" : qUnion([Q0])});
            skCircle(sketch, "E30", {"center": v(0, -100) * mm, "radius": 8 * mm});
            skCircle(sketch, "E31", {"center": v(0, -100) * mm, "radius": 2.5 * mm});
            skLineSegment(sketch, "E32.bottom", {"start": v(63, -115) * mm, "end": v(37, -115) * mm});
            skLineSegment(sketch, "E32.top", {"start": v(63, -85) * mm, "end": v(37, -85) * mm});
            skLineSegment(sketch, "E32.left", {"start": v(65, -113) * mm, "end": v(65, -87) * mm});
            skLineSegment(sketch, "E32.right", {"start": v(35, -113) * mm, "end": v(35, -87) * mm});
            skPoint(sketch, "E32.middle", {"position": v(50, -100) * mm});
            skPoint(sketch, "E33.visualSharp", {"position": v(35, -85) * mm});
            skArc(sketch, "E33.filletArc", {"start": v(37, -85) * mm, "mid": v(35.59, -85.59) * mm, "end": v(35, -87) * mm});
            skPoint(sketch, "E34.visualSharp", {"position": v(65, -85) * mm});
            skArc(sketch, "E34.filletArc", {"start": v(65, -87) * mm, "mid": v(64.41, -85.59) * mm, "end": v(63, -85) * mm});
            skPoint(sketch, "E35.visualSharp", {"position": v(65, -115) * mm});
            skArc(sketch, "E35.filletArc", {"start": v(63, -115) * mm, "mid": v(64.41, -114.41) * mm, "end": v(65, -113) * mm});
            skPoint(sketch, "E36.visualSharp", {"position": v(35, -115) * mm});
            skArc(sketch, "E36.filletArc", {"start": v(35, -113) * mm, "mid": v(35.59, -114.41) * mm, "end": v(37, -115) * mm});
            skLineSegment(sketch, "E37.bottom", {"start": v(62, -112) * mm, "end": v(38, -112) * mm, "construction": true});
            skLineSegment(sketch, "E37.top", {"start": v(62, -88) * mm, "end": v(38, -88) * mm, "construction": true});
            skLineSegment(sketch, "E37.left", {"start": v(62, -112) * mm, "end": v(62, -88) * mm, "construction": true});
            skLineSegment(sketch, "E37.right", {"start": v(38, -112) * mm, "end": v(38, -88) * mm, "construction": true});
            skCircle(sketch, "E38", {"center": v(38, -88) * mm, "radius": 1.5 * mm});
            skCircle(sketch, "E39", {"center": v(62, -88) * mm, "radius": 1.5 * mm});
            skCircle(sketch, "E40", {"center": v(38, -112) * mm, "radius": 1.5 * mm});
            skCircle(sketch, "E41", {"center": v(62, -112) * mm, "radius": 1.5 * mm});
            skCircle(sketch, "E42", {"center": v(50, -100) * mm, "radius": 14.25 * mm});
            skCircle(sketch, "E43", {"center": v(50, -100) * mm, "radius": 7.5 * mm});
            skLineSegment(sketch, "E44", {"start": v(57.5, -100) * mm, "end": v(64.25, -100) * mm});
            skLineSegment(sketch, "E45", {"start": v(57.24, -101.94) * mm, "end": v(63.76, -103.69) * mm});
            skLineSegment(sketch, "E46.1.0", {"start": v(54.68, -94.14) * mm, "end": v(58.88, -88.86) * mm});
            skLineSegment(sketch, "E46.1.1", {"start": v(56.03, -95.55) * mm, "end": v(61.47, -91.54) * mm});
            skLineSegment(sketch, "E46.2.0", {"start": v(48.33, -92.69) * mm, "end": v(46.83, -86.1) * mm});
            skLineSegment(sketch, "E46.2.1", {"start": v(50.28, -92.5) * mm, "end": v(50.53, -85.76) * mm});
            skLineSegment(sketch, "E47.1.3.0", {"start": v(43.24, -96.75) * mm, "end": v(37.16, -93.82) * mm});
            skLineSegment(sketch, "E47.3.3.0", {"start": v(44.32, -95.1) * mm, "end": v(39.2, -90.7) * mm});
            skLineSegment(sketch, "E47.1.4.0", {"start": v(43.24, -103.25) * mm, "end": v(37.16, -106.18) * mm});
            skLineSegment(sketch, "E47.3.4.0", {"start": v(42.63, -101.4) * mm, "end": v(36, -102.65) * mm});
            skLineSegment(sketch, "E48.1.5.0", {"start": v(48.33, -107.31) * mm, "end": v(46.83, -113.9) * mm});
            skLineSegment(sketch, "E48.3.5.0", {"start": v(46.5, -106.63) * mm, "end": v(43.34, -112.6) * mm});
            skLineSegment(sketch, "E48.1.6.0", {"start": v(54.68, -105.86) * mm, "end": v(58.88, -111.14) * mm});
            skLineSegment(sketch, "E48.3.6.0", {"start": v(53, -106.87) * mm, "end": v(55.7, -113.06) * mm});
            skCircle(sketch, "E49", {"center": v(-50, -100) * mm, "radius": 7.5 * mm});
            skCircle(sketch, "E50", {"center": v(-50, -100) * mm, "radius": 4 * mm});
            skCircle(sketch, "E51", {"center": v(-50, -100) * mm, "radius": 7.15 * mm});
            skSolve(sketch);
        }
        {
            var Q0;
            Q0=makeQuery(id+"F12.imprint","IMPRINT",FACE,{"disambiguationData":[TD([[makeQuery(id+"F12.imprint","IMPRINT",EDGE,{"derivedFrom":sQuery(id+"F12.wireOp",EDGE,"E30")}),1.0]])]});
            extrude(context, id + "F13", {"entities" : qUnion([Q0]), "depth" : 5 * mm, "offsetDistance" : 25 * mm});
        }
        {
            var Q0;
            Q0=makeQuery(id+"F12.imprint","IMPRINT",FACE,{"disambiguationData":[TD([[makeQuery(id+"F12.imprint","IMPRINT",EDGE,{"derivedFrom":sQuery(id+"F12.wireOp",EDGE,"E32.bottom")}),-1.0]])]});
            var Q1;
            {var subQ0=sQuery(id+"F12.wireOp",EDGE,"E46.2.0");Q1=makeQuery(id+"F12.imprint","IMPRINT",FACE,{"disambiguationData":[TD([[makeQuery(id+"F12.imprint","IMPRINT",EDGE,{"derivedFrom":subQ0}),-1.0]])]});}
            var Q2;
            {var subQ0=sQuery(id+"F12.wireOp",EDGE,"E46.1.0");Q2=makeQuery(id+"F12.imprint","IMPRINT",FACE,{"disambiguationData":[TD([[makeQuery(id+"F12.imprint","IMPRINT",EDGE,{"derivedFrom":subQ0}),-1.0]])]});}
            var Q3;
            {var subQ0=sQuery(id+"F12.wireOp",EDGE,"E44");Q3=makeQuery(id+"F12.imprint","IMPRINT",FACE,{"disambiguationData":[TD([[makeQuery(id+"F12.imprint","IMPRINT",EDGE,{"derivedFrom":subQ0}),-1.0]])]});}
            var Q4;
            {var subQ0=sQuery(id+"F12.wireOp",EDGE,"E47.1.4.0");Q4=makeQuery(id+"F12.imprint","IMPRINT",FACE,{"disambiguationData":[TD([[makeQuery(id+"F12.imprint","IMPRINT",EDGE,{"derivedFrom":subQ0}),-1.0]])]});}
            var Q5;
            {var subQ0=sQuery(id+"F12.wireOp",EDGE,"E47.1.3.0");Q5=makeQuery(id+"F12.imprint","IMPRINT",FACE,{"disambiguationData":[TD([[makeQuery(id+"F12.imprint","IMPRINT",EDGE,{"derivedFrom":subQ0}),-1.0]])]});}
            var Q6;
            {var subQ0=sQuery(id+"F12.wireOp",EDGE,"E43");var subQ5=makeQuery(id+"F12.imprint","INTERSECT",VERTEX,{"derivedFrom":[subQ0,sQuery(id+"F12.wireOp",EDGE,"E44")]});Q6=makeQuery(id+"F12.imprint","IMPRINT",FACE,{"disambiguationData":[TD([[makeQuery(id+"F12.imprint","IMPRINT",EDGE,{"disambiguationData":[TD([[subQ5,-1.0]])],"derivedFrom":subQ0}),1.0]])]});}
            var Q7;
            {var subQ0=sQuery(id+"F12.wireOp",EDGE,"E48.1.5.0");Q7=makeQuery(id+"F12.imprint","IMPRINT",FACE,{"disambiguationData":[TD([[makeQuery(id+"F12.imprint","IMPRINT",EDGE,{"derivedFrom":subQ0}),-1.0]])]});}
            var Q8;
            {var subQ0=sQuery(id+"F12.wireOp",EDGE,"E48.1.6.0");Q8=makeQuery(id+"F12.imprint","IMPRINT",FACE,{"disambiguationData":[TD([[makeQuery(id+"F12.imprint","IMPRINT",EDGE,{"derivedFrom":subQ0}),-1.0]])]});}
            extrude(context, id + "F14", {"entities" : qUnion([Q0, Q1, Q2, Q3, Q4, Q5, Q6, Q7, Q8]), "depth" : 10 * mm, "offsetDistance" : 25 * mm});
        }
        {
            var Q0;
            Q0=makeQuery(id+"F3.imprint","IMPRINT",FACE,{"disambiguationData":[TD([[makeQuery(id+"F3.imprint","IMPRINT",EDGE,{"derivedFrom":sQuery(id+"F3.wireOp",EDGE,"E27.9.4.0")}),-1.0]])]});
            extrude(context, id + "F15", {"entities" : qUnion([Q0]), "depth" : 250 * mm, "offsetDistance" : 25 * mm});
        }
        {
            var Q0;
            Q0=makeQuery(id+"F3.imprint","IMPRINT",FACE,{"disambiguationData":[TD([[makeQuery(id+"F3.imprint","IMPRINT",EDGE,{"derivedFrom":sQuery(id+"F3.wireOp",EDGE,"E27.9.5.0")}),-1.0]])]});
            extrude(context, id + "F16", {"entities" : qUnion([Q0]), "depth" : 247 * mm, "offsetDistance" : 25 * mm});
        }
        {
            var Q0;
            Q0=makeQuery(id+"F12.imprint","IMPRINT",FACE,{"disambiguationData":[TD([[makeQuery(id+"F12.imprint","IMPRINT",EDGE,{"derivedFrom":sQuery(id+"F12.wireOp",EDGE,"E49")}),1.0]])]});
            var Q1;
            Q1=makeQuery(id+"F12.imprint","IMPRINT",FACE,{"disambiguationData":[TD([[makeQuery(id+"F12.imprint","IMPRINT",EDGE,{"derivedFrom":sQuery(id+"F12.wireOp",EDGE,"E50")}),-1.0]])]});
            extrude(context, id + "F17", {"entities" : qUnion([Q0, Q1]), "endBound" : BoundingType.SYMMETRIC, "depth" : 45 * mm, "offsetDistance" : 25 * mm});
        }
        {
            var Q0;
            Q0=makeQuery(id+"F12.imprint","IMPRINT",FACE,{"disambiguationData":[TD([[makeQuery(id+"F12.imprint","IMPRINT",EDGE,{"derivedFrom":sQuery(id+"F12.wireOp",EDGE,"E49")}),1.0]])]});
            extrude(context, id + "F18", {"entities" : qUnion([Q0]), "operationType" : NewBodyOperationType.REMOVE, "endBound" : BoundingType.SYMMETRIC, "depth" : 35 * mm, "offsetDistance" : 25 * mm});
        }
        {
            var Q0;
            Q0=makeQuery(id+"F12.imprint","IMPRINT",FACE,{"disambiguationData":[TD([[makeQuery(id+"F12.imprint","IMPRINT",EDGE,{"derivedFrom":sQuery(id+"F12.wireOp",EDGE,"E49")}),1.0]])]});
            extrude(context, id + "F19", {"entities" : qUnion([Q0]), "operationType" : NewBodyOperationType.ADD, "endBound" : BoundingType.SYMMETRIC, "depth" : (35 - 2 * 1.1) * mm, "offsetDistance" : 25 * mm});
        }
        {
            var Q0;
            Q0=qCreatedBy(makeId("Top.planeOp"),FACE);
            var sketch = newSketch(context, id + "F20", { "sketchPlane" : qUnion([Q0])});
            skLineSegment(sketch, "E52.bottom", {"start": v(-28.85, -21.15) * mm, "end": v(-71.15, -21.15) * mm});
            skLineSegment(sketch, "E52.top", {"start": v(-28.85, 21.15) * mm, "end": v(-71.15, 21.15) * mm});
            skLineSegment(sketch, "E52.left", {"start": v(-28.85, -21.15) * mm, "end": v(-28.85, 21.15) * mm});
            skLineSegment(sketch, "E52.right", {"start": v(-71.15, -21.15) * mm, "end": v(-71.15, 21.15) * mm});
            skPoint(sketch, "E52.middle", {"position": v(-50, 0) * mm});
            skLineSegment(sketch, "E53.bottom", {"start": v(-34.5, -15.5) * mm, "end": v(-65.5, -15.5) * mm, "construction": true});
            skLineSegment(sketch, "E53.top", {"start": v(-34.5, 15.5) * mm, "end": v(-65.5, 15.5) * mm, "construction": true});
            skLineSegment(sketch, "E53.left", {"start": v(-34.5, -15.5) * mm, "end": v(-34.5, 15.5) * mm, "construction": true});
            skLineSegment(sketch, "E53.right", {"start": v(-65.5, -15.5) * mm, "end": v(-65.5, 15.5) * mm, "construction": true});
            skCircle(sketch, "E54", {"center": v(-34.5, 15.5) * mm, "radius": 1.5 * mm});
            skCircle(sketch, "E55", {"center": v(-34.5, -15.5) * mm, "radius": 1.5 * mm});
            skCircle(sketch, "E56", {"center": v(-65.5, -15.5) * mm, "radius": 1.5 * mm});
            skCircle(sketch, "E57", {"center": v(-65.5, 15.5) * mm, "radius": 1.5 * mm});
            skCircle(sketch, "E58", {"center": v(-50, 0) * mm, "radius": 11 * mm});
            skCircle(sketch, "E59", {"center": v(-50, 0) * mm, "radius": 2.5 * mm});
            skSolve(sketch);
        }
        {
            var Q0;
            Q0=makeQuery(id+"F20.imprint","IMPRINT",FACE,{"disambiguationData":[TD([[makeQuery(id+"F20.imprint","IMPRINT",EDGE,{"derivedFrom":sQuery(id+"F20.wireOp",EDGE,"E52.bottom")}),-1.0]])]});
            var Q1;
            Q1=makeQuery(id+"F20.imprint","IMPRINT",FACE,{"disambiguationData":[TD([[makeQuery(id+"F20.imprint","IMPRINT",EDGE,{"derivedFrom":sQuery(id+"F20.wireOp",EDGE,"E58")}),1.0]])]});
            var Q2;
            Q2=makeQuery(id+"F20.imprint","IMPRINT",FACE,{"disambiguationData":[TD([[makeQuery(id+"F20.imprint","IMPRINT",EDGE,{"derivedFrom":sQuery(id+"F20.wireOp",EDGE,"E59")}),1.0]])]});
            extrude(context, id + "F21", {"entities" : qUnion([Q0, Q1, Q2]), "oppositeDirection" : true, "depth" : 40 * mm, "offsetDistance" : 25 * mm});
        }
        {
            var Q0;
            Q0=makeQuery(id+"F20.imprint","IMPRINT",FACE,{"disambiguationData":[TD([[makeQuery(id+"F20.imprint","IMPRINT",EDGE,{"derivedFrom":sQuery(id+"F20.wireOp",EDGE,"E58")}),1.0]])]});
            extrude(context, id + "F22", {"entities" : qUnion([Q0]), "operationType" : NewBodyOperationType.ADD, "depth" : 2 * mm, "offsetDistance" : 25 * mm});
        }
        {
            var Q0;
            Q0=makeQuery(id+"F20.imprint","IMPRINT",FACE,{"disambiguationData":[TD([[makeQuery(id+"F20.imprint","IMPRINT",EDGE,{"derivedFrom":sQuery(id+"F20.wireOp",EDGE,"E59")}),1.0]])]});
            extrude(context, id + "F23", {"entities" : qUnion([Q0]), "operationType" : NewBodyOperationType.ADD, "depth" : (24 + 2) * mm, "offsetDistance" : 25 * mm});
        }
        {
            var Q0;
            Q0=makeQuery(id+"F20.imprint","IMPRINT",FACE,{"disambiguationData":[TD([[makeQuery(id+"F20.imprint","IMPRINT",EDGE,{"derivedFrom":sQuery(id+"F20.wireOp",EDGE,"E57")}),1.0]])]});
            var Q1;
            Q1=makeQuery(id+"F20.imprint","IMPRINT",FACE,{"disambiguationData":[TD([[makeQuery(id+"F20.imprint","IMPRINT",EDGE,{"derivedFrom":sQuery(id+"F20.wireOp",EDGE,"E54")}),1.0]])]});
            var Q2;
            Q2=makeQuery(id+"F20.imprint","IMPRINT",FACE,{"disambiguationData":[TD([[makeQuery(id+"F20.imprint","IMPRINT",EDGE,{"derivedFrom":sQuery(id+"F20.wireOp",EDGE,"E55")}),1.0]])]});
            var Q3;
            Q3=makeQuery(id+"F20.imprint","IMPRINT",FACE,{"disambiguationData":[TD([[makeQuery(id+"F20.imprint","IMPRINT",EDGE,{"derivedFrom":sQuery(id+"F20.wireOp",EDGE,"E56")}),1.0]])]});
            var Q4;
            Q4=makeQuery(id+"F21.opExtrude","CAP_FACE",FACE,{"disambiguationData":[OSD([sQuery(id+"F20.wireOp",EDGE,"E52.bottom"),sQuery(id+"F20.wireOp",EDGE,"E52.top"),sQuery(id+"F20.wireOp",EDGE,"E52.left"),sQuery(id+"F20.wireOp",EDGE,"E52.right"),sQuery(id+"F20.wireOp",EDGE,"E54"),sQuery(id+"F20.wireOp",EDGE,"E55"),sQuery(id+"F20.wireOp",EDGE,"E56"),sQuery(id+"F20.wireOp",EDGE,"E57")])],"isStart":false});
            extrude(context, id + "F24", {"entities" : qUnion([Q0, Q1, Q2, Q3]), "operationType" : NewBodyOperationType.ADD, "endBound" : BoundingType.UP_TO_SURFACE, "oppositeDirection" : true, "depth" : 25 * mm, "endBoundEntityFace" : qUnion([Q4]), "offsetDistance" : 8 * mm, "offsetOppositeDirection" : true, "hasSecondDirection" : true, "secondDirectionOppositeDirection" : true, "secondDirectionDepth" : 4.5 * mm});
        }
        {
            var Q0;
            Q0=makeQuery(id+"F21.opExtrude","SWEPT_EDGE",EDGE,{"disambiguationData":[OSD([sQuery(id+"F20.wireOp",EDGE,"E52.top"),sQuery(id+"F20.wireOp",EDGE,"E52.right")])]});
            var Q1;
            Q1=makeQuery(id+"F21.opExtrude","SWEPT_EDGE",EDGE,{"disambiguationData":[OSD([sQuery(id+"F20.wireOp",EDGE,"E52.bottom"),sQuery(id+"F20.wireOp",EDGE,"E52.right")])]});
            var Q2;
            Q2=makeQuery(id+"F21.opExtrude","SWEPT_EDGE",EDGE,{"disambiguationData":[OSD([sQuery(id+"F20.wireOp",EDGE,"E52.bottom"),sQuery(id+"F20.wireOp",EDGE,"E52.left")])]});
            var Q3;
            Q3=makeQuery(id+"F21.opExtrude","SWEPT_EDGE",EDGE,{"disambiguationData":[OSD([sQuery(id+"F20.wireOp",EDGE,"E52.top"),sQuery(id+"F20.wireOp",EDGE,"E52.left")])]});
            chamfer(context, id + "F25", {"entities" : qUnion([Q0, Q1, Q2, Q3]), "width" : 5 * mm, "tangentPropagation" : true});
        }
    });
